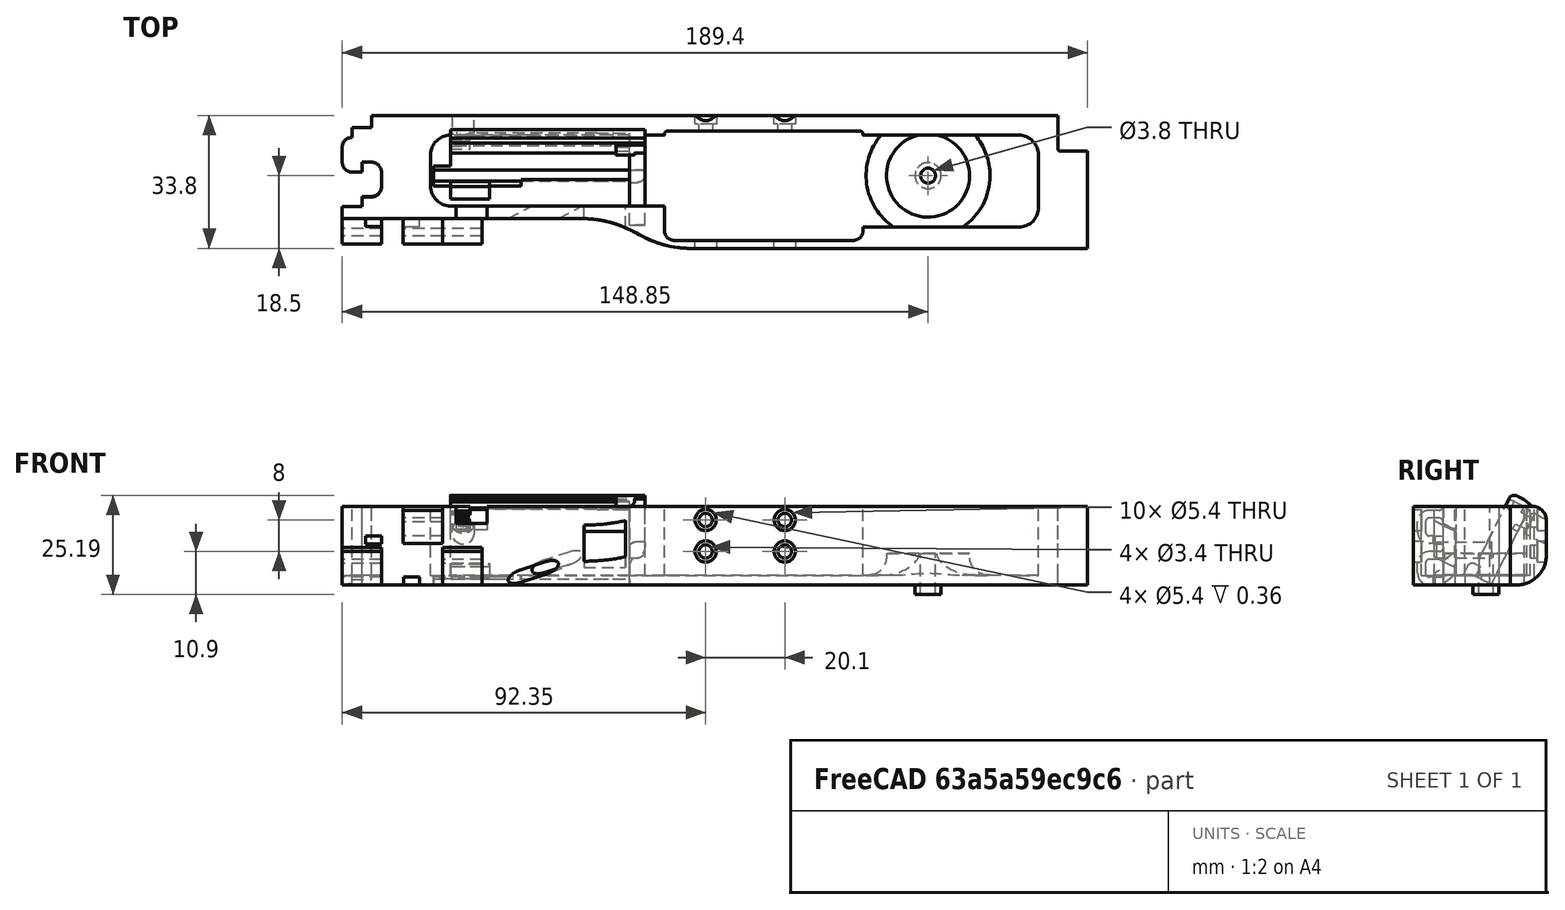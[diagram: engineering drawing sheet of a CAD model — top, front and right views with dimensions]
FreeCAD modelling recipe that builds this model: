
FCSTD DOCUMENT  (FreeCAD 0.19R0.19.2)
Label: v0_9996
License: All rights reserved
LicenseURL: http://en.wikipedia.org/wiki/All_rights_reserved
objects: Sketcher::SketchObject×45, Part::Extrusion×35, Part::MultiFuse×22, Part::Box×19, Part::Cut×16, Part::Fillet×14, App::MeasureDistance×10, Part::Cylinder×4, Part::Revolution×1, Mesh::Feature×1
note: 156 computed .brp shape members not serialized (recipe doc carries the construction recipe); baked Part::Feature solids carry a one-line shape summary decoded from their .brp

FEATURE [Sketcher::SketchObject] Sketch
  FullyConstrained = true
  sketch-geometry (36):
    g0: LineSegment StartX=0 StartY=0 StartZ=0 EndX=154.4 EndY=0 EndZ=0
    g1: LineSegment StartX=154.4 StartY=0 StartZ=0 EndX=154.4 EndY=-7.6 EndZ=0
    g2: LineSegment StartX=32.5209 StartY=-26.2 StartZ=0 EndX=-7.5 EndY=-26.2 EndZ=0
    g3-g7: Circle x5 (B-spline internal-alignment scaffolding for g8; pole/knot coordinates omitted)
    g8: BSplineCurve PolesCount=5 KnotsCount=3 Degree=3 IsPeriodic=0
    g9: GeomPoint X=61.85 Y=-33.8 Z=0
    g10: GeomPoint X=47.185 Y=-29.9 Z=0
    g11: GeomPoint X=32.5209 Y=-26.2 Z=0
    g12: Circle CenterX=121.35 CenterY=-14.3 CenterZ=0 NormalX=0 NormalY=0 NormalZ=1 AngleXU=0 Radius=3.25
    g13: LineSegment StartX=-7.5 StartY=-26.2 StartZ=0 EndX=-27.5 EndY=-26.2 EndZ=0
    g14: LineSegment StartX=-20 StartY=0 StartZ=0 EndX=0 EndY=0 EndZ=0
    g15: LineSegment StartX=-25 StartY=-3.1 StartZ=0 EndX=-20 EndY=-3.1 EndZ=0
    g16: LineSegment StartX=-25 StartY=-3.1 StartZ=0 EndX=-25 EndY=-5.6 EndZ=0
    g17: LineSegment StartX=-27.5 StartY=-8.1 StartZ=0 EndX=-27.5 EndY=-11.85 EndZ=0
    g18: ArcOfCircle CenterX=-25 CenterY=-8.1 CenterZ=0 NormalX=0 NormalY=0 NormalZ=1 AngleXU=0 Radius=2.5 StartAngle=1.5708 EndAngle=3.14159
    g19: LineSegment StartX=-25 StartY=-14.35 StartZ=0 EndX=-22.5 EndY=-14.35 EndZ=0
    g20: ArcOfCircle CenterX=-25 CenterY=-11.85 CenterZ=0 NormalX=0 NormalY=0 NormalZ=1 AngleXU=0 Radius=2.5 StartAngle=3.14159 EndAngle=4.71239
    g21: LineSegment StartX=-22.5 StartY=-14.35 StartZ=0 EndX=-22.5 EndY=-11.85 EndZ=0
    g22: LineSegment StartX=-22.5 StartY=-11.85 StartZ=0 EndX=-20 EndY=-11.85 EndZ=0
    g23: ArcOfCircle CenterX=-20 CenterY=-14.35 CenterZ=0 NormalX=0 NormalY=0 NormalZ=1 AngleXU=0 Radius=2.5 StartAngle=8e-16 EndAngle=1.5708
    g24: LineSegment StartX=-17.5 StartY=-14.35 StartZ=0 EndX=-17.5 EndY=-18.1 EndZ=0
    g25: ArcOfCircle CenterX=-20 CenterY=-18.1 CenterZ=0 NormalX=0 NormalY=0 NormalZ=1 AngleXU=0 Radius=2.5 StartAngle=4.71239 EndAngle=6.28319
    g26: LineSegment StartX=-22.5 StartY=-20.6 StartZ=0 EndX=-20 EndY=-20.6 EndZ=0
    g27: LineSegment StartX=-22.5 StartY=-20.6 StartZ=0 EndX=-22.5 EndY=-23.1 EndZ=0
    g28: LineSegment StartX=-27.5 StartY=-23.1 StartZ=0 EndX=-22.5 EndY=-23.1 EndZ=0
    g29: LineSegment StartX=-20 StartY=-3.1 StartZ=0 EndX=-20 EndY=0 EndZ=0
    g30: LineSegment StartX=-27.5 StartY=-23.1 StartZ=0 EndX=-27.5 EndY=-26.2 EndZ=0
    g31: LineSegment StartX=154.4 StartY=-7.6 StartZ=0 EndX=154.4 EndY=-8.6 EndZ=0
    g32: ArcOfCircle CenterX=154.9 CenterY=-8.6 CenterZ=0 NormalX=0 NormalY=0 NormalZ=1 AngleXU=0 Radius=0.5 StartAngle=3.14159 EndAngle=4.71239
    g33: LineSegment StartX=154.9 StartY=-9.1 StartZ=0 EndX=161.9 EndY=-9.1 EndZ=0
    g34: LineSegment StartX=161.9 StartY=-9.1 StartZ=0 EndX=161.9 EndY=-33.8 EndZ=0
    g35: LineSegment StartX=161.9 StartY=-33.8 StartZ=0 EndX=61.85 EndY=-33.8 EndZ=0
  constraints (72):
    c: PointOnObject(g0,g-2)
    c: Horizontal(g0)
    c: Distance(g0) = 154.4
    c: DistanceY(g-1,g0) = 0
    c: Vertical(g1)
    c: Distance(g1) = 7.6
    c: Coincident(g1,g0)
    c: Horizontal(g2)
    c: Block(g2)
    c: Weight(g3) = 1
    c: Coincident(g8,g2)
    c: InternalAlignment(g3-g7 -> g8) x5
    c: InternalAlignment(g9,g8)
    c: InternalAlignment(g10,g8)
    c: InternalAlignment(g11,g8)
    c: Block(g12)
    c: Coincident(g13,g2)
    c: Horizontal(g13)
    c: Distance(g13) = 20
    c: Horizontal(g14)
    c: Distance(g14) = 20
    c: Coincident(g14,g0)
    c: Horizontal(g15)
    c: Vertical(g16)
    c: Coincident(g16,g15)
    c: Vertical(g17)
    c: Coincident(g18,g16)
    c: Block(g18)
    c: Coincident(g17,g18)
    c: Horizontal(g19)
    c: Coincident(g20,g17)
    c: Block(g20)
    c: Block(g19)
    c: Vertical(g21)
    c: Coincident(g21,g19)
    c: Horizontal(g22)
    c: Coincident(g22,g21)
    c: Coincident(g23,g22)
    c: Vertical(g24)
    c: Block(g23)
    c: Coincident(g24,g23)
    c: Coincident(g25,g24)
    c: Block(g25)
    c: Horizontal(g26)
    c: Coincident(g26,g25)
    c: Vertical(g27)
    c: Coincident(g27,g26)
    c: Horizontal(g28)
    c: Coincident(g28,g27)
    c: Block(g15)
    c: Block(g28)
    c: Coincident(g29,g15)
    c: Coincident(g29,g14)
    c: Vertical(g29)
    c: Coincident(g30,g28)
    c: Coincident(g30,g13)
    c: Vertical(g30)
    c: Vertical(g31)
    c: Distance(g31) = 1
    c: Coincident(g31,g1)
    c: Coincident(g32,g31)
    c: Block(g32)
    c: Coincident(g33,g32)
    c: Horizontal(g33)
    c: Coincident(g34,g33)
    c: Vertical(g34)
    c: Block(g34)
    c: Coincident(g35,g34)
    c: Horizontal(g35)
    c: Block(g35)
    c: Coincident(g8,g35)
    c: Block(g8)
FEATURE [Part::Extrusion] Extrude  label="mainBodyBaseExtrude"
  Base = -> Sketch
  Dir = (0,0,1)
  DirMode = 2
  FaceMakerClass = Part::FaceMakerBullseye
  LengthFwd = 2.4
  LengthRev = 0
  Solid = true
  Symmetric = false
FEATURE [Sketcher::SketchObject] Sketch001
  FullyConstrained = true
  sketch-geometry (75):
    g0: ArcOfCircle CenterX=144.4 CenterY=-10 CenterZ=0 NormalX=0 NormalY=0 NormalZ=1 AngleXU=0 Radius=5 StartAngle=4.345e-13 EndAngle=1.5708
    g1: LineSegment StartX=32.5209 StartY=-26.2 StartZ=0 EndX=-7.49911 EndY=-26.2 EndZ=0
    g2: LineSegment StartX=0 StartY=0 StartZ=0 EndX=154.4 EndY=0 EndZ=0
    g3-g7: Circle x5 (B-spline internal-alignment scaffolding for g8; pole/knot coordinates omitted)
    g8: BSplineCurve PolesCount=5 KnotsCount=3 Degree=3 IsPeriodic=0
    g9: GeomPoint X=61.85 Y=-33.8 Z=0
    g10: GeomPoint X=47.1857 Y=-29.9 Z=0
    g11: GeomPoint X=32.5209 Y=-26.2 Z=0
    g12: LineSegment StartX=154.4 StartY=0 StartZ=0 EndX=154.4 EndY=-7.6 EndZ=0
    g13: LineSegment StartX=20 StartY=-5 StartZ=0 EndX=54.35 EndY=-5 EndZ=0
    g14: LineSegment StartX=104.85 StartY=-5 StartZ=0 EndX=144.4 EndY=-5 EndZ=0
    g15: LineSegment StartX=54.35 StartY=-23 StartZ=0 EndX=20 EndY=-23 EndZ=0
    g16: LineSegment StartX=-27.4991 StartY=-26.2 StartZ=0 EndX=-7.49911 EndY=-26.2 EndZ=0
    g17: LineSegment StartX=-20 StartY=0 StartZ=0 EndX=0 EndY=0 EndZ=0
    g18: LineSegment StartX=-27.4991 StartY=-23.2 StartZ=0 EndX=-22.5 EndY=-23.2 EndZ=0
    g19: LineSegment StartX=-22.5 StartY=-20.7 StartZ=0 EndX=-22.5 EndY=-23.2 EndZ=0
    g20: LineSegment StartX=-22.5 StartY=-20.7 StartZ=0 EndX=-20 EndY=-20.7 EndZ=0
    g21: ArcOfCircle CenterX=-20 CenterY=-18.2 CenterZ=0 NormalX=0 NormalY=0 NormalZ=1 AngleXU=0 Radius=2.5 StartAngle=4.71239 EndAngle=6.28319
    g22: LineSegment StartX=-17.5 StartY=-14.4 StartZ=0 EndX=-17.5 EndY=-18.2 EndZ=0
    g23: ArcOfCircle CenterX=-20 CenterY=-14.4 CenterZ=0 NormalX=0 NormalY=0 NormalZ=1 AngleXU=0 Radius=2.5 StartAngle=9e-16 EndAngle=1.5708
    g24: LineSegment StartX=-22.5 StartY=-11.9 StartZ=0 EndX=-20 EndY=-11.9 EndZ=0
    g25: LineSegment StartX=-22.5 StartY=-14.4 StartZ=0 EndX=-22.5 EndY=-11.9 EndZ=0
    g26: LineSegment StartX=-25 StartY=-14.4 StartZ=0 EndX=-22.5 EndY=-14.4 EndZ=0
    g27: ArcOfCircle CenterX=-25 CenterY=-11.9 CenterZ=0 NormalX=0 NormalY=0 NormalZ=1 AngleXU=0 Radius=2.5 StartAngle=3.14159 EndAngle=4.71239
    g28: LineSegment StartX=-27.5 StartY=-8.1 StartZ=0 EndX=-27.5 EndY=-11.9 EndZ=0
    g29: ArcOfCircle CenterX=-25 CenterY=-8.1 CenterZ=0 NormalX=0 NormalY=0 NormalZ=1 AngleXU=0 Radius=2.5 StartAngle=1.5708 EndAngle=3.14159
    g30: LineSegment StartX=-25 StartY=-3.1 StartZ=0 EndX=-25 EndY=-5.6 EndZ=0
    g31: LineSegment StartX=-20 StartY=-3.1 StartZ=0 EndX=-25 EndY=-3.1 EndZ=0
    g32: LineSegment StartX=-20 StartY=0 StartZ=0 EndX=-20 EndY=-3.1 EndZ=0
    g33: LineSegment StartX=-27.4991 StartY=-26.2 StartZ=0 EndX=-27.4991 EndY=-23.2 EndZ=0
    g34: LineSegment StartX=4.09e-14 StartY=-5 StartZ=0 EndX=20 EndY=-5 EndZ=0
    g35: ArcOfCircle CenterX=7.1e-15 CenterY=-18 CenterZ=0 NormalX=0 NormalY=0 NormalZ=1 AngleXU=0 Radius=5 StartAngle=3.14159 EndAngle=4.71239
    g36: ArcOfCircle CenterX=4.26e-14 CenterY=-10 CenterZ=0 NormalX=0 NormalY=0 NormalZ=1 AngleXU=0 Radius=5 StartAngle=1.5708 EndAngle=3.14159
    g37: LineSegment StartX=-5 StartY=-18 StartZ=0 EndX=-5 EndY=-10 EndZ=0
    g38: LineSegment StartX=6.2e-15 StartY=-23 StartZ=0 EndX=20 EndY=-23 EndZ=0
    g39: LineSegment StartX=154.4 StartY=-7.6 StartZ=0 EndX=154.4 EndY=-8.6 EndZ=0
    g40: LineSegment StartX=154.9 StartY=-9.1 StartZ=0 EndX=161.9 EndY=-9.1 EndZ=0
    g41: ArcOfCircle CenterX=154.9 CenterY=-8.6 CenterZ=0 NormalX=0 NormalY=0 NormalZ=1 AngleXU=0 Radius=0.5 StartAngle=3.14159 EndAngle=4.71299
    g42: LineSegment StartX=104.85 StartY=-28.3916 StartZ=0 EndX=144.408 EndY=-28.3916 EndZ=0
    g43: LineSegment StartX=149.4 StartY=-10 StartZ=0 EndX=149.4 EndY=-23.4 EndZ=0
    g44: ArcOfCircle CenterX=144.408 CenterY=-23.4 CenterZ=0 NormalX=0 NormalY=0 NormalZ=1 AngleXU=0 Radius=4.99164 StartAngle=4.71239 EndAngle=6.28319
    g45: LineSegment StartX=104.85 StartY=-28.3916 StartZ=0 EndX=104.85 EndY=-28.7833 EndZ=0
    g46: LineSegment StartX=54.35 StartY=-28.7916 StartZ=0 EndX=54.35 EndY=-23 EndZ=0
    g47: LineSegment StartX=161.9 StartY=-33.8 StartZ=0 EndX=161.9 EndY=-9.1 EndZ=0
    g48: LineSegment StartX=61.85 StartY=-33.8 StartZ=0 EndX=161.9 EndY=-33.8 EndZ=0
    g49: Circle CenterX=54.35 CenterY=-28.7916 CenterZ=0 NormalX=0 NormalY=0 NormalZ=1 AngleXU=0 Radius=1
    g50: Circle CenterX=54.35 CenterY=-31.7916 CenterZ=0 NormalX=0 NormalY=0 NormalZ=1 AngleXU=0 Radius=1
    g51: Circle CenterX=57.35 CenterY=-31.7916 CenterZ=0 NormalX=0 NormalY=0 NormalZ=1 AngleXU=0 Radius=1
    g52: BSplineCurve PolesCount=3 KnotsCount=2 Degree=2 IsPeriodic=0
    g53: GeomPoint X=54.35 Y=-28.7916 Z=0
    g54: GeomPoint X=57.35 Y=-31.7916 Z=0
    g55: Circle CenterX=104.85 CenterY=-28.7833 CenterZ=0 NormalX=0 NormalY=0 NormalZ=1 AngleXU=0 Radius=1
    g56: Circle CenterX=104.85 CenterY=-31.7916 CenterZ=0 NormalX=0 NormalY=0 NormalZ=1 AngleXU=0 Radius=1
    g57: Circle CenterX=101.85 CenterY=-31.7916 CenterZ=0 NormalX=0 NormalY=0 NormalZ=1 AngleXU=0 Radius=1
    g58: BSplineCurve PolesCount=3 KnotsCount=2 Degree=2 IsPeriodic=0
    g59: GeomPoint X=104.85 Y=-28.7833 Z=0
    g60: GeomPoint X=101.85 Y=-31.7916 Z=0
    g61: LineSegment StartX=57.35 StartY=-31.7916 StartZ=0 EndX=101.85 EndY=-31.7916 EndZ=0
    g62: Circle CenterX=54.35 CenterY=-5 CenterZ=0 NormalX=0 NormalY=0 NormalZ=1 AngleXU=0 Radius=1
    g63: Circle CenterX=54.35 CenterY=-4 CenterZ=0 NormalX=0 NormalY=0 NormalZ=1 AngleXU=0 Radius=1
    g64: Circle CenterX=55.15 CenterY=-4 CenterZ=0 NormalX=0 NormalY=0 NormalZ=1 AngleXU=0 Radius=1
    g65: BSplineCurve PolesCount=3 KnotsCount=2 Degree=2 IsPeriodic=0
    g66: GeomPoint X=54.35 Y=-5 Z=0
    g67: GeomPoint X=55.15 Y=-4 Z=0
    g68: Circle CenterX=104.85 CenterY=-5 CenterZ=0 NormalX=0 NormalY=0 NormalZ=1 AngleXU=0 Radius=1
    g69: Circle CenterX=104.85 CenterY=-4 CenterZ=0 NormalX=0 NormalY=0 NormalZ=1 AngleXU=0 Radius=1
    g70: Circle CenterX=104.05 CenterY=-4 CenterZ=0 NormalX=0 NormalY=0 NormalZ=1 AngleXU=0 Radius=1
    g71: BSplineCurve PolesCount=3 KnotsCount=2 Degree=2 IsPeriodic=0
    g72: GeomPoint X=104.85 Y=-5 Z=0
    g73: GeomPoint X=104.05 Y=-4 Z=0
    g74: LineSegment StartX=104.05 StartY=-4 StartZ=0 EndX=55.15 EndY=-4 EndZ=0
  constraints (156):
    c: PointOnObject(g2,g-2)
    c: DistanceY(g-1,g2) = 0
    c: Block(g0)
    c: Horizontal(g1)
    c: Distance(g1) = 40.02
    c: Horizontal(g2)
    c: Block(g2)
    c: Weight(g3) = 1
    c: Equal(g3, g4-g7) x4
    c: Coincident(g8,g1)
    c: InternalAlignment(g3-g7 -> g8) x5
    c: InternalAlignment(g9,g8)
    c: InternalAlignment(g10,g8)
    c: InternalAlignment(g11,g8)
    c: Vertical(g12)
    c: Coincident(g12,g2)
    c: Distance(g12) = 7.6
    c: Block(g12)
    c: Horizontal(g13)
    c: Coincident(g14,g0)
    c: Horizontal(g14)
    c: Horizontal(g15)
    c: Horizontal(g16)
    c: Distance(g16) = 20
    c: Coincident(g1,g16)
    c: Horizontal(g17)
    c: Distance(g17) = 20
    c: Coincident(g17,g2)
    c: Horizontal(g31)
    c: Vertical(g30)
    c: Coincident(g29,g30)
    c: Vertical(g28)
    c: Block(g29)
    c: Coincident(g27,g28)
    c: Block(g27)
    c: Horizontal(g26)
    c: Coincident(g26,g27)
    c: Vertical(g25)
    c: Coincident(g25,g26)
    c: Horizontal(g24)
    c: Coincident(g23,g24)
    c: Block(g23)
    c: Vertical(g22)
    c: Coincident(g21,g22)
    c: Block(g21)
    c: Horizontal(g20)
    c: Coincident(g20,g21)
    c: Vertical(g19)
    c: Coincident(g19,g20)
    c: Horizontal(g18)
    c: Coincident(g18,g19)
    c: Coincident(g32,g17)
    c: Coincident(g32,g31)
    c: Vertical(g32)
    c: Coincident(g33,g16)
    c: Coincident(g33,g18)
    c: Vertical(g33)
    c: Block(g33)
    c: Block(g18)
    c: Block(g22)
    c: Block(g26)
    c: Block(g25)
    c: Block(g24)
    c: Block(g28)
    c: Block(g31)
    c: Block(g30)
    c: Horizontal(g34)
    c: Distance(g34) = 20
    c: Block(g35)
    c: Block(g36)
    c: Coincident(g37,g35)
    c: Coincident(g37,g36)
    c: Vertical(g37)
    c: Coincident(g38,g35)
    c: Coincident(g38,g15)
    c: Horizontal(g38)
    c: Block(g38)
    c: Block(g34)
    c: Block(g13)
    c: Vertical(g39)
    c: Distance(g39) = 1
    c: Coincident(g39,g12)
    c: Horizontal(g40)
    c: Coincident(g41,g39)
    c: Coincident(g41,g40)
    c: Block(g39)
    c: Block(g41)
    c: Horizontal(g42)
    c: Vertical(g43)
    c: Distance(g43) = 13.4
    c: Coincident(g43,g0)
    c: Block(g42)
    c: Block(g43)
    c: Coincident(g44,g43)
    c: Coincident(g44,g42)
    c: Block(g44)
    c: Distance(g15) = 34.35
    c: Coincident(g45,g42)
    c: Vertical(g45)
    c: Coincident(g46,g15)
    c: Vertical(g46)
    c: Coincident(g47,g40)
    c: Vertical(g47)
    c: Block(g47)
    c: Coincident(g48,g47)
    c: Horizontal(g48)
    c: Block(g48)
    c: Coincident(g8,g48)
    c: Block(g8)
    c: Coincident(g52,g46)
    c: Weight(g49) = 1
    c: Equal(g49,g50)
    c: Equal(g49,g51)
    c: InternalAlignment(g49,g52)
    c: InternalAlignment(g50,g52)
    c: InternalAlignment(g51,g52)
    c: InternalAlignment(g53,g52)
    c: InternalAlignment(g54,g52)
    c: Coincident(g58,g45)
    c: Weight(g55) = 1
    c: Equal(g55,g56)
    c: Equal(g55,g57)
    c: InternalAlignment(g55,g58)
    c: InternalAlignment(g56,g58)
    c: InternalAlignment(g57,g58)
    c: InternalAlignment(g59,g58)
    c: InternalAlignment(g60,g58)
    c: Block(g58)
    c: Block(g52)
    c: Coincident(g61,g52)
    c: Coincident(g61,g58)
    c: Horizontal(g61)
    c: Block(g14)
    c: Coincident(g65,g13)
    c: Weight(g62) = 1
    c: Equal(g62,g63)
    c: Equal(g62,g64)
    c: InternalAlignment(g62,g65)
    c: InternalAlignment(g63,g65)
    c: InternalAlignment(g64,g65)
    c: InternalAlignment(g66,g65)
    c: InternalAlignment(g67,g65)
    c: Block(g65)
    c: Coincident(g71,g14)
    c: Weight(g68) = 1
    c: Equal(g68,g69)
    c: Equal(g68,g70)
    c: InternalAlignment(g68,g71)
    c: InternalAlignment(g69,g71)
    c: InternalAlignment(g70,g71)
    c: InternalAlignment(g72,g71)
    c: InternalAlignment(g73,g71)
    c: Block(g71)
    c: Coincident(g74,g71)
    c: Coincident(g74,g65)
    c: Horizontal(g74)
FEATURE [Sketcher::SketchObject] Sketch005
  FullyConstrained = true
  Placement = pos=(0,0,0) rot=(1,0,0;1.5708rad)
  sketch-geometry (4):
    g0: Circle CenterX=84.95 CenterY=16.5 CenterZ=0 NormalX=0 NormalY=0 NormalZ=1 AngleXU=0 Radius=1.7
    g1: Circle CenterX=84.95 CenterY=8.5 CenterZ=0 NormalX=0 NormalY=0 NormalZ=1 AngleXU=0 Radius=1.7
    g2: Circle CenterX=64.85 CenterY=8.5 CenterZ=0 NormalX=0 NormalY=0 NormalZ=1 AngleXU=0 Radius=1.7
    g3: Circle CenterX=64.85 CenterY=16.5 CenterZ=0 NormalX=0 NormalY=0 NormalZ=1 AngleXU=0 Radius=1.7
  constraints (4):
    c: Block(g0)
    c: Block(g1)
    c: Block(g2)
    c: Block(g3)
FEATURE [Part::Extrusion] Extrude004  label="removeFromMainBodyToCreateScrewHolesForSolenoidExtrude004"
  Base = -> Sketch005
  Dir = (0,-1,1.1e-15)
  DirMode = 2
  FaceMakerClass = Part::FaceMakerBullseye
  LengthFwd = 10
  LengthRev = 0
  Solid = true
  Symmetric = false
FEATURE [Sketcher::SketchObject] Sketch004
  FullyConstrained = true
  Placement = pos=(0,0,0) rot=(1,0,0;1.5708rad)
  sketch-geometry (12):
    g0: LineSegment StartX=15.75 StartY=2.5 StartZ=0 EndX=15.75 EndY=0 EndZ=0
    g1: Circle CenterX=15.75 CenterY=2.5 CenterZ=0 NormalX=0 NormalY=0 NormalZ=1 AngleXU=0 Radius=1
    g2: Circle CenterX=10.55 CenterY=2.5 CenterZ=0 NormalX=0 NormalY=0 NormalZ=1 AngleXU=0 Radius=1
    g3: Circle CenterX=10.55 CenterY=8 CenterZ=0 NormalX=0 NormalY=0 NormalZ=1 AngleXU=0 Radius=1
    g4: BSplineCurve PolesCount=3 KnotsCount=2 Degree=2 IsPeriodic=0
    g5: GeomPoint X=15.75 Y=2.5 Z=0
    g6: GeomPoint X=10.55 Y=8 Z=0
    g7: LineSegment StartX=1.9 StartY=8 StartZ=0 EndX=10.55 EndY=8 EndZ=0
    g8: LineSegment StartX=1.9 StartY=-2.4 StartZ=0 EndX=1.9 EndY=8 EndZ=0
    g9: LineSegment StartX=3.30092 StartY=-2.4 StartZ=0 EndX=3.30092 EndY=0 EndZ=0
    g10: LineSegment StartX=15.75 StartY=0 StartZ=0 EndX=3.30092 EndY=0 EndZ=0
    g11: LineSegment StartX=3.30092 StartY=-2.4 StartZ=0 EndX=1.9 EndY=-2.4 EndZ=0
  constraints (26):
    c: Vertical(g0)
    c: Distance(g0) = 2.5
    c: Coincident(g4,g0)
    c: Weight(g1) = 1
    c: Equal(g1,g2)
    c: Equal(g1,g3)
    c: InternalAlignment(g1,g4)
    c: InternalAlignment(g2,g4)
    c: InternalAlignment(g3,g4)
    c: InternalAlignment(g5,g4)
    c: InternalAlignment(g6,g4)
    c: Block(g4)
    c: Coincident(g7,g4)
    c: Horizontal(g7)
    c: Vertical(g8)
    c: Coincident(g8,g7)
    c: Block(g8)
    c: Vertical(g9)
    c: Coincident(g10,g0)
    c: PointOnObject(g10,g-1)
    c: Horizontal(g10)
    c: Coincident(g10,g9)
    c: Block(g9)
    c: Coincident(g11,g9)
    c: Coincident(g11,g8)
    c: Horizontal(g11)
FEATURE [Sketcher::SketchObject] Sketch007
  FullyConstrained = true
  Placement = pos=(0,-14.3,2.37) rot=(-1,0,0;2.03453rad)
  sketch-geometry (6):
    g0: LineSegment StartX=0 StartY=0 StartZ=0 EndX=45.5 EndY=0 EndZ=0
    g1: LineSegment StartX=0 StartY=0 StartZ=0 EndX=0 EndY=-21.2 EndZ=0
    g2: LineSegment StartX=45.5 StartY=0 StartZ=0 EndX=49.5 EndY=0 EndZ=0
    g3: LineSegment StartX=49.5 StartY=0 StartZ=0 EndX=49.5 EndY=-21.2 EndZ=0
    g4: LineSegment StartX=49.5 StartY=-21.2 StartZ=0 EndX=0 EndY=-21.2 EndZ=0
    g5: Circle CenterX=3.25 CenterY=-18.05 CenterZ=0 NormalX=0 NormalY=0 NormalZ=1 AngleXU=0 Radius=1.6
  constraints (15):
    c: Coincident(g0,g-1)
    c: Horizontal(g0)
    c: Distance(g0) = 45.5
    c: Coincident(g1,g0)
    c: Vertical(g1)
    c: Horizontal(g2)
    c: Distance(g2) = 4
    c: Coincident(g2,g0)
    c: Coincident(g3,g2)
    c: Vertical(g3)
    c: Block(g3)
    c: Coincident(g4,g3)
    c: Horizontal(g4)
    c: Coincident(g4,g1)
    c: Block(g5)
FEATURE [Part::Extrusion] Extrude005  label="solenoidDriverHolderExtrude005"
  Base = -> Sketch007
  Dir = (0,0.894389,-0.447291)
  DirMode = 2
  FaceMakerClass = Part::FaceMakerBullseye
  LengthFwd = 10
  LengthRev = 0
  Placement = pos=(0,0,-2) rot=(0,0,1;0rad)
  Solid = true
  Symmetric = false
FEATURE [Sketcher::SketchObject] Sketch008
  FullyConstrained = false
  Placement = pos=(0,-4.3,-2.6) rot=(-1,0,0;2.03453rad)
  sketch-geometry (1):
    g0: Circle CenterX=42.25 CenterY=-3.15 CenterZ=0 NormalX=0 NormalY=0 NormalZ=1 AngleXU=0 Radius=4.5
FEATURE [Sketcher::SketchObject] Sketch009
  FullyConstrained = true
  Placement = pos=(0,-4.3,-2.6) rot=(-1,0,0;2.03453rad)
  sketch-geometry (1):
    g0: Circle CenterX=3.25 CenterY=-18.0217 CenterZ=0 NormalX=0 NormalY=0 NormalZ=1 AngleXU=0 Radius=2.8
  constraints (1):
    c: Block(g0)
FEATURE [Sketcher::SketchObject] Sketch010
  FullyConstrained = true
  Placement = pos=(0,-14.3,2.37) rot=(-1,0,0;2.03453rad)
  sketch-geometry (1):
    g0: Circle CenterX=3.25 CenterY=-18.05 CenterZ=0 NormalX=0 NormalY=0 NormalZ=1 AngleXU=0 Radius=1.6
  constraints (1):
    c: Block(g0)
FEATURE [Part::Extrusion] Extrude008  label="removeFromScrewHole3"
  Base = -> Sketch010
  Dir = (0,0.894389,-0.447291)
  DirMode = 2
  FaceMakerClass = Part::FaceMakerBullseye
  LengthFwd = -25
  LengthRev = 0
  Placement = pos=(0,4,-4) rot=(0,0,1;0rad)
  Solid = true
  Symmetric = false
FEATURE [Sketcher::SketchObject] Sketch011
  FullyConstrained = true
  Placement = pos=(0,-14.3,2.37) rot=(-1,0,0;2.03453rad)
  sketch-geometry (4):
    g0: LineSegment StartX=49.5 StartY=-21.2 StartZ=0 EndX=49.5 EndY=-22.8 EndZ=0
    g1: LineSegment StartX=49.5 StartY=-22.8 StartZ=0 EndX=0.002238 EndY=-22.8 EndZ=0
    g2: LineSegment StartX=0.002238 StartY=-21.2 StartZ=0 EndX=0.002238 EndY=-22.8 EndZ=0
    g3: LineSegment StartX=49.5 StartY=-21.2 StartZ=0 EndX=0.002238 EndY=-21.2 EndZ=0
  constraints (10):
    c: Vertical(g0)
    c: Distance(g0) = 1.6
    c: Coincident(g1,g0)
    c: Horizontal(g1)
    c: Vertical(g2)
    c: Coincident(g2,g1)
    c: Coincident(g3,g0)
    c: Coincident(g3,g2)
    c: Horizontal(g3)
    c: Block(g3)
FEATURE [Part::Extrusion] Extrude009  label="solenoidDriverTopLipFront"
  Base = -> Sketch011
  Dir = (0,0.894389,-0.447291)
  DirMode = 2
  FaceMakerClass = Part::FaceMakerBullseye
  LengthFwd = -2
  LengthRev = 0
  Placement = pos=(0,-2.9,-0.35) rot=(0,0,1;0rad)
  Solid = true
  Symmetric = false
FEATURE [Sketcher::SketchObject] Sketch012
  FullyConstrained = true
  Placement = pos=(0,-14.3,2.37) rot=(-1,0,0;2.03453rad)
  sketch-geometry (4):
    g0: LineSegment StartX=49.5 StartY=-21.2 StartZ=0 EndX=49.5 EndY=-22.8 EndZ=0
    g1: LineSegment StartX=49.5 StartY=-22.8 StartZ=0 EndX=0.002238 EndY=-22.8 EndZ=0
    g2: LineSegment StartX=0.002238 StartY=-21.2 StartZ=0 EndX=0.002238 EndY=-22.8 EndZ=0
    g3: LineSegment StartX=49.5 StartY=-21.2 StartZ=0 EndX=0.002238 EndY=-21.2 EndZ=0
  constraints (10):
    c: Vertical(g0)
    c: Distance(g0) = 1.6
    c: Coincident(g1,g0)
    c: Horizontal(g1)
    c: Vertical(g2)
    c: Coincident(g2,g1)
    c: Coincident(g3,g0)
    c: Coincident(g3,g2)
    c: Horizontal(g3)
    c: Block(g3)
FEATURE [Part::Extrusion] Extrude010  label="solenoidDriverTopLipLowerExtrude010"
  Base = -> Sketch012
  Dir = (0,0.894389,-0.447291)
  DirMode = 2
  FaceMakerClass = Part::FaceMakerBullseye
  LengthFwd = 5.05
  LengthRev = 0
  Solid = true
  Symmetric = false
FEATURE [Sketcher::SketchObject] Sketch015
  FullyConstrained = true
  Placement = pos=(0,-14.3,2.37) rot=(-1,0,0;2.03453rad)
  sketch-geometry (4):
    g0: LineSegment StartX=0 StartY=1.5 StartZ=0 EndX=0 EndY=0 EndZ=0
    g1: LineSegment StartX=0 StartY=1.5 StartZ=0 EndX=5 EndY=1.5 EndZ=0
    g2: LineSegment StartX=5 StartY=1.5 StartZ=0 EndX=5 EndY=0 EndZ=0
    g3: LineSegment StartX=0 StartY=0 StartZ=0 EndX=5 EndY=0 EndZ=0
  constraints (13):
    c: Vertical(g0)
    c: Distance(g0) = 1.5
    c: Horizontal(g1)
    c: Distance(g1) = 5
    c: Coincident(g1,g0)
    c: Vertical(g2)
    c: Distance(g2) = 1.5
    c: Coincident(g2,g1)
    c: Block(g1)
    c: Block(g2)
    c: Block(g0)
    c: Coincident(g3,g0)
    c: Coincident(g3,g2)
FEATURE [Part::Extrusion] Extrude013  label="solenoidDriverBottomLipTopExtrude012"
  Base = -> Sketch015
  Dir = (0,0.894389,-0.447291)
  DirMode = 2
  FaceMakerClass = Part::FaceMakerBullseye
  LengthFwd = -6.5
  LengthRev = 0
  Placement = pos=(0,-14.15,19.65) rot=(1,0,0;1.5708rad)
  Solid = true
  Symmetric = false
FEATURE [Sketcher::SketchObject] Sketch016
  FullyConstrained = true
  Placement = pos=(0,0,0) rot=(1,0,0;1.5708rad)
  sketch-geometry (4):
    g0: Circle CenterX=84.15 CenterY=16.5 CenterZ=0 NormalX=0 NormalY=0 NormalZ=1 AngleXU=0 Radius=2.7
    g1: Circle CenterX=64.05 CenterY=16.5 CenterZ=0 NormalX=0 NormalY=0 NormalZ=1 AngleXU=0 Radius=2.7
    g2: Circle CenterX=64.05 CenterY=8.5 CenterZ=0 NormalX=0 NormalY=0 NormalZ=1 AngleXU=0 Radius=2.7
    g3: Circle CenterX=84.15 CenterY=8.5 CenterZ=0 NormalX=0 NormalY=0 NormalZ=1 AngleXU=0 Radius=2.7
  constraints (4):
    c: Block(g0)
    c: Block(g1)
    c: Block(g3)
    c: Block(g2)
FEATURE [Part::Extrusion] Extrude014  label="removeFromMainBodyToCreateScrewHoleCounterSinks"
  Base = -> Sketch016
  Dir = (0,-1,1.1e-15)
  DirMode = 2
  FaceMakerClass = Part::FaceMakerBullseye
  LengthFwd = 1.9
  LengthRev = 0
  Placement = pos=(0.8,-0.36,0) rot=(0,0,1;0rad)
  Solid = true
  Symmetric = false
FEATURE [Part::Extrusion] Extrude015  label="removeFromScrewHole2Extrude007"
  Base = -> Sketch009
  Dir = (0,0.894389,-0.447291)
  DirMode = 2
  FaceMakerClass = Part::FaceMakerBullseye
  LengthFwd = 10
  LengthRev = 0
  Placement = pos=(0,-8,2) rot=(0,0,1;0rad)
  Solid = true
  Symmetric = false
FEATURE [Sketcher::SketchObject] Sketch017
  FullyConstrained = true
  Placement = pos=(0,-14.3,2.37) rot=(-1,0,0;2.03453rad)
  sketch-geometry (4):
    g0: LineSegment StartX=0 StartY=1.5 StartZ=0 EndX=0 EndY=0 EndZ=0
    g1: LineSegment StartX=0 StartY=1.5 StartZ=0 EndX=5 EndY=1.5 EndZ=0
    g2: LineSegment StartX=5 StartY=1.5 StartZ=0 EndX=5 EndY=0 EndZ=0
    g3: LineSegment StartX=0 StartY=0 StartZ=0 EndX=5 EndY=0 EndZ=0
  constraints (13):
    c: Vertical(g0)
    c: Distance(g0) = 1.5
    c: Horizontal(g1)
    c: Distance(g1) = 5
    c: Coincident(g1,g0)
    c: Vertical(g2)
    c: Distance(g2) = 1.5
    c: Coincident(g2,g1)
    c: Block(g1)
    c: Block(g2)
    c: Block(g0)
    c: Coincident(g3,g0)
    c: Coincident(g3,g2)
FEATURE [Part::Extrusion] Extrude016  label="solenoidDriverBottomLipTopExtrude013"
  Base = -> Sketch017
  Dir = (0,0.894389,-0.447291)
  DirMode = 2
  FaceMakerClass = Part::FaceMakerBullseye
  LengthFwd = -6.5
  LengthRev = 0
  Placement = pos=(0,-15.45,20.3) rot=(1,0,0;1.5708rad)
  Solid = true
  Symmetric = false
FEATURE [Part::Fillet] Fillet005  label="solenoidDriverBottomLipTopFillet005"
  Base = -> Extrude016
  Edges = 1 edges r=1.4: [Edge6]
FEATURE [Sketcher::SketchObject] Sketch018
  FullyConstrained = true
  Placement = pos=(38.5,-14.3,2.37) rot=(-1,0,0;2.03453rad)
  sketch-geometry (4):
    g0: LineSegment StartX=11 StartY=0 StartZ=0 EndX=11 EndY=1.5 EndZ=0
    g1: LineSegment StartX=11 StartY=0 StartZ=0 EndX=3.6 EndY=0 EndZ=0
    g2: LineSegment StartX=3.6 StartY=0 StartZ=0 EndX=3.6 EndY=1.5 EndZ=0
    g3: LineSegment StartX=11 StartY=1.5 StartZ=0 EndX=3.6 EndY=1.5 EndZ=0
  constraints (12):
    c: PointOnObject(g0,g-1)
    c: Vertical(g0)
    c: Distance(g0) = 1.5
    c: Horizontal(g1)
    c: Distance(g1) = 7.4
    c: Coincident(g1,g0)
    c: Block(g0)
    c: Coincident(g2,g1)
    c: Vertical(g2)
    c: Coincident(g3,g0)
    c: Horizontal(g3)
    c: Coincident(g2,g3)
FEATURE [Part::Extrusion] Extrude017
  Base = -> Sketch018
  Dir = (0,0.894389,-0.447291)
  DirMode = 2
  FaceMakerClass = Part::FaceMakerBullseye
  LengthFwd = 4
  LengthRev = 0
  Placement = pos=(0,-8.212,34.025) rot=(1,0,0;1.5708rad)
  Solid = true
  Symmetric = false
FEATURE [Sketcher::SketchObject] Sketch019
  FullyConstrained = true
  Placement = pos=(0,0,0) rot=(1,0,0;1.5708rad)
  sketch-geometry (4):
    g0: Circle CenterX=84.95 CenterY=8.5 CenterZ=0 NormalX=0 NormalY=0 NormalZ=1 AngleXU=0 Radius=2.7
    g1: Circle CenterX=64.85 CenterY=8.5 CenterZ=0 NormalX=0 NormalY=0 NormalZ=1 AngleXU=0 Radius=2.7
    g2: Circle CenterX=64.85 CenterY=16.5 CenterZ=0 NormalX=0 NormalY=0 NormalZ=1 AngleXU=0 Radius=2.7
    g3: Circle CenterX=84.95 CenterY=16.5 CenterZ=0 NormalX=0 NormalY=0 NormalZ=1 AngleXU=0 Radius=2.7
  constraints (4):
    c: Block(g3)
    c: Block(g2)
    c: Block(g0)
    c: Block(g1)
FEATURE [Part::Extrusion] Extrude019  label="removeSolenoidAdjusterHoles"
  Base = -> Sketch019
  Dir = (0,-1,1.1e-15)
  DirMode = 2
  FaceMakerClass = Part::FaceMakerBullseye
  LengthFwd = 6
  LengthRev = 0
  Placement = pos=(0,-30,0) rot=(0,0,1;0rad)
  Solid = true
  Symmetric = false
FEATURE [Sketcher::SketchObject] Sketch020
  FullyConstrained = true
  Placement = pos=(0,-14.3,2.37) rot=(-1,0,0;2.03453rad)
  sketch-geometry (6):
    g0: LineSegment StartX=45.5 StartY=-21.2 StartZ=0 EndX=49.5 EndY=-21.2 EndZ=0
    g1: LineSegment StartX=45.5 StartY=0 StartZ=0 EndX=49.5 EndY=0 EndZ=0
    g2: LineSegment StartX=49.5 StartY=0 StartZ=0 EndX=49.5 EndY=-21.2 EndZ=0
    g3: LineSegment StartX=4 StartY=0 StartZ=0 EndX=4 EndY=-21.2 EndZ=0
    g4: LineSegment StartX=45.5 StartY=-21.2 StartZ=0 EndX=4 EndY=-21.2 EndZ=0
    g5: LineSegment StartX=4 StartY=0 StartZ=0 EndX=45.5 EndY=0 EndZ=0
  constraints (16):
    c: Horizontal(g0)
    c: Distance(g0) = 4
    c: Horizontal(g1)
    c: Distance(g1) = 4
    c: Coincident(g2,g1)
    c: Coincident(g2,g0)
    c: Vertical(g2)
    c: Block(g2)
    c: Vertical(g3)
    c: Coincident(g4,g0)
    c: Horizontal(g4)
    c: Coincident(g4,g3)
    c: Coincident(g5,g1)
    c: Horizontal(g5)
    c: Block(g3)
    c: Block(g5)
FEATURE [Part::Box] Box  label="Cube"
  AttacherType = Attacher::AttachEngine3D
  Height = 10
  Length = 190
  Placement = pos=(-30,0,0) rot=(0,0,1;0rad)
  Width = 10
FEATURE [Part::Fillet] Fillet008
  Base = -> Box
  Edges = 1 edges r=7.5: [Edge11]
FEATURE [Part::Box] Box001  label="Cube001"
  AttacherType = Attacher::AttachEngine3D
  Height = 10
  Length = 190
  Placement = pos=(-35,0,0) rot=(0,0,1;0rad)
  Width = 10
FEATURE [Part::Cut] Cut  label="filletMain"
  Base = -> Box001
  Placement = pos=(0,-10,0) rot=(0,0,1;0rad)
  Tool = -> Fillet008
FEATURE [Part::Box] Box002  label="Cube002"
  AttacherType = Attacher::AttachEngine3D
  Height = 30
  Length = 190
  Placement = pos=(-20,0,0) rot=(0,0,1;0rad)
  Width = 10
FEATURE [Part::Box] Box003  label="Cube003"
  AttacherType = Attacher::AttachEngine3D
  Height = 10
  Length = 190
  Placement = pos=(-90,-50,-10) rot=(0,0,1;0rad)
  Width = 50
FEATURE [Sketcher::SketchObject] Sketch021
  FullyConstrained = true
  Placement = pos=(0,-14.3,2.37) rot=(-1,0,0;2.03453rad)
  sketch-geometry (6):
    g0: LineSegment StartX=41.65 StartY=-3.15 StartZ=0 EndX=38.95 EndY=-3.15 EndZ=0
    g1: LineSegment StartX=36.25 StartY=-3.15 StartZ=0 EndX=38.95 EndY=-3.15 EndZ=0
    g2: LineSegment StartX=41.65 StartY=-3.15 StartZ=0 EndX=41.65 EndY=-7.15 EndZ=0
    g3: LineSegment StartX=38.95 StartY=-7.15 StartZ=0 EndX=41.65 EndY=-7.15 EndZ=0
    g4: LineSegment StartX=38.95 StartY=-7.15 StartZ=0 EndX=36.25 EndY=-7.15 EndZ=0
    g5: LineSegment StartX=36.25 StartY=-3.15 StartZ=0 EndX=36.25 EndY=-7.15 EndZ=0
  constraints (16):
    c: Horizontal(g0)
    c: Distance(g0) = 2.7
    c: Horizontal(g1)
    c: Distance(g1) = 2.7
    c: Coincident(g1,g0)
    c: Block(g0)
    c: Coincident(g2,g0)
    c: Vertical(g2)
    c: Horizontal(g3)
    c: Coincident(g3,g2)
    c: Horizontal(g4)
    c: Coincident(g5,g1)
    c: Vertical(g5)
    c: Coincident(g5,g4)
    c: Block(g3)
    c: Block(g4)
FEATURE [Sketcher::SketchObject] Sketch022
  FullyConstrained = true
  Placement = pos=(0,-14.3,2.37) rot=(-1,0,0;2.03453rad)
  sketch-geometry (6):
    g0: LineSegment StartX=41.65 StartY=-3.15 StartZ=0 EndX=38.95 EndY=-3.15 EndZ=0
    g1: LineSegment StartX=36.25 StartY=-3.15 StartZ=0 EndX=38.95 EndY=-3.15 EndZ=0
    g2: LineSegment StartX=41.65 StartY=-3.15 StartZ=0 EndX=41.65 EndY=-7.15 EndZ=0
    g3: LineSegment StartX=38.95 StartY=-7.15 StartZ=0 EndX=41.65 EndY=-7.15 EndZ=0
    g4: LineSegment StartX=38.95 StartY=-7.15 StartZ=0 EndX=36.25 EndY=-7.15 EndZ=0
    g5: LineSegment StartX=36.25 StartY=-3.15 StartZ=0 EndX=36.25 EndY=-7.15 EndZ=0
  constraints (16):
    c: Horizontal(g0)
    c: Distance(g0) = 2.7
    c: Horizontal(g1)
    c: Distance(g1) = 2.7
    c: Coincident(g1,g0)
    c: Block(g0)
    c: Coincident(g2,g0)
    c: Vertical(g2)
    c: Horizontal(g3)
    c: Coincident(g3,g2)
    c: Horizontal(g4)
    c: Coincident(g5,g1)
    c: Vertical(g5)
    c: Coincident(g5,g4)
    c: Block(g3)
    c: Block(g4)
FEATURE [Sketcher::SketchObject] Sketch024
  FullyConstrained = true
  Placement = pos=(0,-14.3,2.37) rot=(-1,0,0;2.03453rad)
  sketch-geometry (4):
    g0: LineSegment StartX=49.5 StartY=-21.2 StartZ=0 EndX=49.5 EndY=-22.8 EndZ=0
    g1: LineSegment StartX=49.5 StartY=-22.8 StartZ=0 EndX=0.002238 EndY=-22.8 EndZ=0
    g2: LineSegment StartX=0.002238 StartY=-21.2 StartZ=0 EndX=0.002238 EndY=-22.8 EndZ=0
    g3: LineSegment StartX=49.5 StartY=-21.2 StartZ=0 EndX=0.002238 EndY=-21.2 EndZ=0
  constraints (10):
    c: Vertical(g0)
    c: Distance(g0) = 1.6
    c: Coincident(g1,g0)
    c: Horizontal(g1)
    c: Vertical(g2)
    c: Coincident(g2,g1)
    c: Coincident(g3,g0)
    c: Coincident(g3,g2)
    c: Horizontal(g3)
    c: Block(g3)
FEATURE [Sketcher::SketchObject] Sketch025
  FullyConstrained = true
  Placement = pos=(0,-14.3,2.37) rot=(-1,0,0;2.03453rad)
  sketch-geometry (4):
    g0: LineSegment StartX=0 StartY=1.5 StartZ=0 EndX=0 EndY=0 EndZ=0
    g1: LineSegment StartX=0 StartY=1.5 StartZ=0 EndX=5 EndY=1.5 EndZ=0
    g2: LineSegment StartX=5 StartY=1.5 StartZ=0 EndX=5 EndY=0 EndZ=0
    g3: LineSegment StartX=0 StartY=0 StartZ=0 EndX=5 EndY=0 EndZ=0
  constraints (13):
    c: Vertical(g0)
    c: Distance(g0) = 1.5
    c: Horizontal(g1)
    c: Distance(g1) = 5
    c: Coincident(g1,g0)
    c: Vertical(g2)
    c: Distance(g2) = 1.5
    c: Coincident(g2,g1)
    c: Block(g1)
    c: Block(g2)
    c: Block(g0)
    c: Coincident(g3,g0)
    c: Coincident(g3,g2)
FEATURE [Part::Extrusion] Extrude022  label="solenoidDriverBottomLipTopExtrude014"
  Base = -> Sketch025
  Dir = (0,0.894389,-0.447291)
  DirMode = 2
  FaceMakerClass = Part::FaceMakerBullseye
  LengthFwd = -6.5
  LengthRev = 0
  Placement = pos=(0,-15.45,20.3) rot=(1,0,0;1.5708rad)
  Solid = true
  Symmetric = false
FEATURE [Part::Fillet] Fillet013  label="solenoidDriverBottomLipTopFillet006"
  Base = -> Extrude022
  Edges = 1 edges r=1.4: [Edge6]
  Placement = pos=(5,0,0) rot=(0,0,1;0rad)
FEATURE [Sketcher::SketchObject] Sketch026
  FullyConstrained = true
  Placement = pos=(0,-14.3,2.37) rot=(-1,0,0;2.03453rad)
  sketch-geometry (4):
    g0: LineSegment StartX=0 StartY=1.5 StartZ=0 EndX=0 EndY=0 EndZ=0
    g1: LineSegment StartX=0 StartY=1.5 StartZ=0 EndX=5 EndY=1.5 EndZ=0
    g2: LineSegment StartX=5 StartY=1.5 StartZ=0 EndX=5 EndY=0 EndZ=0
    g3: LineSegment StartX=0 StartY=0 StartZ=0 EndX=5 EndY=0 EndZ=0
  constraints (13):
    c: Vertical(g0)
    c: Distance(g0) = 1.5
    c: Horizontal(g1)
    c: Distance(g1) = 5
    c: Coincident(g1,g0)
    c: Vertical(g2)
    c: Distance(g2) = 1.5
    c: Coincident(g2,g1)
    c: Block(g1)
    c: Block(g2)
    c: Block(g0)
    c: Coincident(g3,g0)
    c: Coincident(g3,g2)
FEATURE [Part::Extrusion] Extrude023  label="solenoidDriverBottomLipTopExtrude015"
  Base = -> Sketch026
  Dir = (0,0.894389,-0.447291)
  DirMode = 2
  FaceMakerClass = Part::FaceMakerBullseye
  LengthFwd = -6.5
  LengthRev = 0
  Placement = pos=(5,-14.15,19.65) rot=(1,0,0;1.5708rad)
  Solid = true
  Symmetric = false
FEATURE [Sketcher::SketchObject] Sketch027
  FullyConstrained = true
  Placement = pos=(0,-14.3,2.37) rot=(-1,0,0;2.03453rad)
  sketch-geometry (5):
    g0: LineSegment StartX=45.5 StartY=-21.2 StartZ=0 EndX=49.5 EndY=-21.2 EndZ=0
    g1: LineSegment StartX=49.5 StartY=0 StartZ=0 EndX=49.5 EndY=-21.2 EndZ=0
    g2: LineSegment StartX=49.5 StartY=0 StartZ=0 EndX=49.5 EndY=1.6 EndZ=0
    g3: LineSegment StartX=45.5 StartY=-21.2 StartZ=0 EndX=45.5 EndY=1.6 EndZ=0
    g4: LineSegment StartX=49.5 StartY=1.6 StartZ=0 EndX=45.5 EndY=1.6 EndZ=0
  constraints (14):
    c: Horizontal(g0)
    c: Distance(g0) = 4
    c: Coincident(g1,g0)
    c: Vertical(g1)
    c: Block(g1)
    c: Vertical(g2)
    c: Distance(g2) = 1.6
    c: Block(g2)
    c: Coincident(g3,g0)
    c: Vertical(g3)
    c: Coincident(g4,g2)
    c: Horizontal(g4)
    c: Block(g0)
    c: Coincident(g3,g4)
FEATURE [Part::Extrusion] Extrude024
  Base = -> Sketch027
  Dir = (0,0.894389,-0.447291)
  DirMode = 2
  FaceMakerClass = Part::FaceMakerBullseye
  LengthFwd = 6.34
  LengthRev = 0
  Placement = pos=(0,-5.59,1) rot=(0,0,1;0rad)
  Solid = true
  Symmetric = false
FEATURE [Part::Fillet] Fillet014  label="solenoidDriverSideBarFillet014"
  Base = -> Extrude024
  Edges = 1 edges r=1.4: [Edge14]
  Placement = pos=(0,0.9,-0.45) rot=(0,0,1;0rad)
FEATURE [Part::Revolution] Revolve  label="mainScrewStandRevolve"
  Angle = 360
  Axis = (0,0,1)
  Base = (0,0,0)
  FaceMakerClass = Part::FaceMakerBullseye
  Placement = pos=(121.35,-15.3,0) rot=(0,0,1;0rad)
  Solid = true
  Source = -> Sketch004
  Symmetric = false
FEATURE [Part::Extrusion] Extrude021  label="solenoidDriverTopLipLowerExtrude011"
  Base = -> Sketch024
  Dir = (0,0.894389,-0.447291)
  DirMode = 2
  FaceMakerClass = Part::FaceMakerBullseye
  LengthFwd = 5.05
  LengthRev = 0
  Solid = true
  Symmetric = false
FEATURE [Part::Fillet] Fillet012  label="solenoidDriverTopLipLowerFillet004"
  Base = -> Extrude021
  Edges = 1 edges r=1.2: [Edge7]
  Placement = pos=(0,-0.9,-1.35) rot=(0,0,1;0rad)
FEATURE [Part::Fillet] Fillet003  label="solenoidDriverTopLipLowerFillet003"
  Base = -> Extrude010
  Edges = 1 edges r=1.2: [Edge7]
  Placement = pos=(0,-3,-0.3) rot=(0,0,1;0rad)
FEATURE [Part::Extrusion] Extrude025  label="mainBodyUpperExtrude025"
  Base = -> Sketch001
  Dir = (0,0,1)
  DirMode = 2
  FaceMakerClass = Part::FaceMakerBullseye
  LengthFwd = 20
  LengthRev = 0
  Solid = true
  Symmetric = false
FEATURE [Part::MultiFuse] Fusion  label="solenoidDriverBottomLipFusion"
  Placement = pos=(0,-1.6,0) rot=(0,0,1;0rad)
  Shapes = -> [Fillet005,Fillet013,Extrude023,Extrude013]
FEATURE [Sketcher::SketchObject] Sketch028
  FullyConstrained = true
  Placement = pos=(0,-14.3,2.37) rot=(-1,0,0;2.03453rad)
  sketch-geometry (4):
    g0: LineSegment StartX=0 StartY=1.5 StartZ=0 EndX=0 EndY=0 EndZ=0
    g1: LineSegment StartX=0 StartY=1.5 StartZ=0 EndX=5 EndY=1.5 EndZ=0
    g2: LineSegment StartX=5 StartY=1.5 StartZ=0 EndX=5 EndY=0 EndZ=0
    g3: LineSegment StartX=0 StartY=0 StartZ=0 EndX=5 EndY=0 EndZ=0
  constraints (13):
    c: Vertical(g0)
    c: Distance(g0) = 1.5
    c: Horizontal(g1)
    c: Distance(g1) = 5
    c: Coincident(g1,g0)
    c: Vertical(g2)
    c: Distance(g2) = 1.5
    c: Coincident(g2,g1)
    c: Block(g1)
    c: Block(g2)
    c: Block(g0)
    c: Coincident(g3,g0)
    c: Coincident(g3,g2)
FEATURE [Part::Extrusion] Extrude026  label="solenoidDriverBottomLipTopExtrude016"
  Base = -> Sketch028
  Dir = (0,0.894389,-0.447291)
  DirMode = 2
  FaceMakerClass = Part::FaceMakerBullseye
  LengthFwd = -6.5
  LengthRev = 0
  Placement = pos=(5,-14.15,19.65) rot=(1,0,0;1.5708rad)
  Solid = true
  Symmetric = false
FEATURE [Sketcher::SketchObject] Sketch029
  FullyConstrained = true
  Placement = pos=(0,-14.3,2.37) rot=(-1,0,0;2.03453rad)
  sketch-geometry (4):
    g0: LineSegment StartX=0 StartY=1.5 StartZ=0 EndX=0 EndY=0 EndZ=0
    g1: LineSegment StartX=0 StartY=1.5 StartZ=0 EndX=5 EndY=1.5 EndZ=0
    g2: LineSegment StartX=5 StartY=1.5 StartZ=0 EndX=5 EndY=0 EndZ=0
    g3: LineSegment StartX=0 StartY=0 StartZ=0 EndX=5 EndY=0 EndZ=0
  constraints (13):
    c: Vertical(g0)
    c: Distance(g0) = 1.5
    c: Horizontal(g1)
    c: Distance(g1) = 5
    c: Coincident(g1,g0)
    c: Vertical(g2)
    c: Distance(g2) = 1.5
    c: Coincident(g2,g1)
    c: Block(g1)
    c: Block(g2)
    c: Block(g0)
    c: Coincident(g3,g0)
    c: Coincident(g3,g2)
FEATURE [Part::Extrusion] Extrude027  label="solenoidDriverBottomLipTopExtrude017"
  Base = -> Sketch029
  Dir = (0,0.894389,-0.447291)
  DirMode = 2
  FaceMakerClass = Part::FaceMakerBullseye
  LengthFwd = -6.5
  LengthRev = 0
  Placement = pos=(0,-14.15,19.65) rot=(1,0,0;1.5708rad)
  Solid = true
  Symmetric = false
FEATURE [Sketcher::SketchObject] Sketch030
  FullyConstrained = true
  Placement = pos=(0,-14.3,2.37) rot=(-1,0,0;2.03453rad)
  sketch-geometry (4):
    g0: LineSegment StartX=0 StartY=1.5 StartZ=0 EndX=0 EndY=0 EndZ=0
    g1: LineSegment StartX=0 StartY=1.5 StartZ=0 EndX=5 EndY=1.5 EndZ=0
    g2: LineSegment StartX=5 StartY=1.5 StartZ=0 EndX=5 EndY=0 EndZ=0
    g3: LineSegment StartX=0 StartY=0 StartZ=0 EndX=5 EndY=0 EndZ=0
  constraints (13):
    c: Vertical(g0)
    c: Distance(g0) = 1.5
    c: Horizontal(g1)
    c: Distance(g1) = 5
    c: Coincident(g1,g0)
    c: Vertical(g2)
    c: Distance(g2) = 1.5
    c: Coincident(g2,g1)
    c: Block(g1)
    c: Block(g2)
    c: Block(g0)
    c: Coincident(g3,g0)
    c: Coincident(g3,g2)
FEATURE [Sketcher::SketchObject] Sketch031
  FullyConstrained = true
  Placement = pos=(0,-14.3,2.37) rot=(-1,0,0;2.03453rad)
  sketch-geometry (6):
    g0: LineSegment StartX=45.5 StartY=-21.2 StartZ=0 EndX=49.5 EndY=-21.2 EndZ=0
    g1: LineSegment StartX=45.5 StartY=0 StartZ=0 EndX=49.5 EndY=0 EndZ=0
    g2: LineSegment StartX=49.5 StartY=0 StartZ=0 EndX=49.5 EndY=-21.2 EndZ=0
    g3: LineSegment StartX=4 StartY=0 StartZ=0 EndX=4 EndY=-21.2 EndZ=0
    g4: LineSegment StartX=45.5 StartY=-21.2 StartZ=0 EndX=4 EndY=-21.2 EndZ=0
    g5: LineSegment StartX=4 StartY=0 StartZ=0 EndX=45.5 EndY=0 EndZ=0
  constraints (16):
    c: Horizontal(g0)
    c: Distance(g0) = 4
    c: Horizontal(g1)
    c: Distance(g1) = 4
    c: Coincident(g2,g1)
    c: Coincident(g2,g0)
    c: Vertical(g2)
    c: Block(g2)
    c: Vertical(g3)
    c: Coincident(g4,g0)
    c: Horizontal(g4)
    c: Coincident(g4,g3)
    c: Coincident(g5,g1)
    c: Horizontal(g5)
    c: Block(g3)
    c: Block(g5)
FEATURE [Part::Extrusion] Extrude028  label="removeFromSolenoidDriverMainExtrude021"
  Base = -> Sketch031
  Dir = (0,0.894389,-0.447291)
  DirMode = 2
  FaceMakerClass = Part::FaceMakerBullseye
  LengthFwd = 3.1
  LengthRev = 0
  Placement = pos=(-4,-2.42,-0.8) rot=(0,0,1;0rad)
  Solid = true
  Symmetric = false
FEATURE [Part::Extrusion] Extrude029  label="solenoidDriverBottomLipTopExtrude018"
  Base = -> Sketch030
  Dir = (0,0.894389,-0.447291)
  DirMode = 2
  FaceMakerClass = Part::FaceMakerBullseye
  LengthFwd = -6.5
  LengthRev = 0
  Placement = pos=(5,-14.15,19.65) rot=(1,0,0;1.5708rad)
  Solid = true
  Symmetric = false
FEATURE [Sketcher::SketchObject] Sketch032
  FullyConstrained = true
  Placement = pos=(0,-14.3,2.37) rot=(-1,0,0;2.03453rad)
  sketch-geometry (4):
    g0: LineSegment StartX=0 StartY=1.5 StartZ=0 EndX=0 EndY=0 EndZ=0
    g1: LineSegment StartX=0 StartY=1.5 StartZ=0 EndX=5 EndY=1.5 EndZ=0
    g2: LineSegment StartX=5 StartY=1.5 StartZ=0 EndX=5 EndY=0 EndZ=0
    g3: LineSegment StartX=0 StartY=0 StartZ=0 EndX=5 EndY=0 EndZ=0
  constraints (13):
    c: Vertical(g0)
    c: Distance(g0) = 1.5
    c: Horizontal(g1)
    c: Distance(g1) = 5
    c: Coincident(g1,g0)
    c: Vertical(g2)
    c: Distance(g2) = 1.5
    c: Coincident(g2,g1)
    c: Block(g1)
    c: Block(g2)
    c: Block(g0)
    c: Coincident(g3,g0)
    c: Coincident(g3,g2)
FEATURE [Part::Extrusion] Extrude030  label="solenoidDriverBottomLipTopExtrude019"
  Base = -> Sketch032
  Dir = (0,0.894389,-0.447291)
  DirMode = 2
  FaceMakerClass = Part::FaceMakerBullseye
  LengthFwd = -6.5
  LengthRev = 0
  Placement = pos=(0,-14.15,19.65) rot=(1,0,0;1.5708rad)
  Solid = true
  Symmetric = false
FEATURE [Part::MultiFuse] Fusion004
  Placement = pos=(0,1.4,2.65) rot=(0,0,1;0rad)
  Shapes = -> [Extrude029,Extrude030]
FEATURE [Part::MultiFuse] Fusion003
  Placement = pos=(-2.3,0,0) rot=(0,0,1;0rad)
  Shapes = -> [Extrude028,Fusion004]
FEATURE [Sketcher::SketchObject] Sketch033
  FullyConstrained = true
  Placement = pos=(0,-14.3,2.37) rot=(-1,0,0;2.03453rad)
  sketch-geometry (4):
    g0: LineSegment StartX=0 StartY=1.5 StartZ=0 EndX=0 EndY=0 EndZ=0
    g1: LineSegment StartX=0 StartY=1.5 StartZ=0 EndX=5 EndY=1.5 EndZ=0
    g2: LineSegment StartX=5 StartY=1.5 StartZ=0 EndX=5 EndY=0 EndZ=0
    g3: LineSegment StartX=0 StartY=0 StartZ=0 EndX=5 EndY=0 EndZ=0
  constraints (13):
    c: Vertical(g0)
    c: Distance(g0) = 1.5
    c: Horizontal(g1)
    c: Distance(g1) = 5
    c: Coincident(g1,g0)
    c: Vertical(g2)
    c: Distance(g2) = 1.5
    c: Coincident(g2,g1)
    c: Block(g1)
    c: Block(g2)
    c: Block(g0)
    c: Coincident(g3,g0)
    c: Coincident(g3,g2)
FEATURE [Sketcher::SketchObject] Sketch034
  FullyConstrained = true
  Placement = pos=(0,-14.3,2.37) rot=(-1,0,0;2.03453rad)
  sketch-geometry (4):
    g0: LineSegment StartX=0 StartY=1.5 StartZ=0 EndX=4 EndY=1.5 EndZ=0
    g1: LineSegment StartX=4 StartY=1.5 StartZ=0 EndX=4 EndY=-2.5 EndZ=0
    g2: LineSegment StartX=4 StartY=-2.5 StartZ=0 EndX=0 EndY=-2.5 EndZ=0
    g3: LineSegment StartX=0 StartY=1.5 StartZ=0 EndX=0 EndY=-2.5 EndZ=0
  constraints (11):
    c: Horizontal(g0)
    c: Distance(g0) = 4
    c: Block(g0)
    c: Coincident(g1,g0)
    c: Vertical(g1)
    c: Distance(g1) = 4
    c: Coincident(g2,g1)
    c: Horizontal(g2)
    c: Distance(g2) = 4
    c: Coincident(g3,g0)
    c: Coincident(g3,g2)
FEATURE [Part::Extrusion] Extrude020  label="removeFromSolenoidDriverMainExtrude020"
  Base = -> Sketch020
  Dir = (0,0.894389,-0.447291)
  DirMode = 2
  FaceMakerClass = Part::FaceMakerBullseye
  LengthFwd = 3.1
  LengthRev = 0
  Placement = pos=(-4,-2.42,-0.8) rot=(0,0,1;0rad)
  Solid = true
  Symmetric = false
FEATURE [Part::Fillet] Fillet
  Base = -> Fusion003
  Edges = 1 edges r=10: [Edge5]
  Placement = pos=(-2,0,0) rot=(0,0,1;0rad)
FEATURE [Part::MultiFuse] Fusion001
  Placement = pos=(0,1.4,2.65) rot=(0,0,1;0rad)
  Shapes = -> [Extrude026,Extrude027]
FEATURE [Part::MultiFuse] Fusion002
  Shapes = -> [Extrude020,Fusion001]
FEATURE [Sketcher::SketchObject] Sketch035
  FullyConstrained = true
  Placement = pos=(0,-14.3,2.37) rot=(-1,0,0;2.03453rad)
  sketch-geometry (4):
    g0: LineSegment StartX=0 StartY=1.5 StartZ=0 EndX=0 EndY=0 EndZ=0
    g1: LineSegment StartX=0 StartY=1.5 StartZ=0 EndX=5 EndY=1.5 EndZ=0
    g2: LineSegment StartX=5 StartY=1.5 StartZ=0 EndX=5 EndY=0 EndZ=0
    g3: LineSegment StartX=0 StartY=0 StartZ=0 EndX=5 EndY=0 EndZ=0
  constraints (13):
    c: Vertical(g0)
    c: Distance(g0) = 1.5
    c: Horizontal(g1)
    c: Distance(g1) = 5
    c: Coincident(g1,g0)
    c: Vertical(g2)
    c: Distance(g2) = 1.5
    c: Coincident(g2,g1)
    c: Block(g1)
    c: Block(g2)
    c: Block(g0)
    c: Coincident(g3,g0)
    c: Coincident(g3,g2)
FEATURE [Sketcher::SketchObject] Sketch036
  FullyConstrained = true
  Placement = pos=(0,-14.3,2.37) rot=(-1,0,0;2.03453rad)
  sketch-geometry (4):
    g0: LineSegment StartX=0 StartY=1.5 StartZ=0 EndX=0 EndY=0 EndZ=0
    g1: LineSegment StartX=0 StartY=1.5 StartZ=0 EndX=5 EndY=1.5 EndZ=0
    g2: LineSegment StartX=5 StartY=1.5 StartZ=0 EndX=5 EndY=0 EndZ=0
    g3: LineSegment StartX=0 StartY=0 StartZ=0 EndX=5 EndY=0 EndZ=0
  constraints (13):
    c: Vertical(g0)
    c: Distance(g0) = 1.5
    c: Horizontal(g1)
    c: Distance(g1) = 5
    c: Coincident(g1,g0)
    c: Vertical(g2)
    c: Distance(g2) = 1.5
    c: Coincident(g2,g1)
    c: Block(g1)
    c: Block(g2)
    c: Block(g0)
    c: Coincident(g3,g0)
    c: Coincident(g3,g2)
FEATURE [Part::Extrusion] Extrude031  label="solenoidDriverBottomLipTopExtrude020"
  Base = -> Sketch035
  Dir = (0,0.894389,-0.447291)
  DirMode = 2
  FaceMakerClass = Part::FaceMakerBullseye
  LengthFwd = -6.5
  LengthRev = 0
  Placement = pos=(5,-14.15,19.65) rot=(1,0,0;1.5708rad)
  Solid = true
  Symmetric = false
FEATURE [Part::Extrusion] Extrude032  label="solenoidDriverBottomLipTopExtrude021"
  Base = -> Sketch036
  Dir = (0,0.894389,-0.447291)
  DirMode = 2
  FaceMakerClass = Part::FaceMakerBullseye
  LengthFwd = -6.5
  LengthRev = 0
  Placement = pos=(0,-14.15,19.65) rot=(1,0,0;1.5708rad)
  Solid = true
  Symmetric = false
FEATURE [Part::MultiFuse] Fusion009
  Placement = pos=(8,1.4,2.65) rot=(0,0,1;0rad)
  Shapes = -> [Extrude031,Extrude032]
FEATURE [Part::MultiFuse] Fusion010  label="removeFromSolenoidDriver"
  Shapes = -> [Fusion009,Fillet,Fusion002]
FEATURE [Sketcher::SketchObject] Sketch037
  FullyConstrained = true
  Placement = pos=(0,0,0) rot=(1,0,0;1.5708rad)
  sketch-geometry (4):
    g0: Circle CenterX=64.05 CenterY=16.5 CenterZ=0 NormalX=0 NormalY=0 NormalZ=1 AngleXU=0 Radius=2.7
    g1: Circle CenterX=64.05 CenterY=8.5 CenterZ=0 NormalX=0 NormalY=0 NormalZ=1 AngleXU=0 Radius=2.7
    g2: Circle CenterX=84.15 CenterY=8.5 CenterZ=0 NormalX=0 NormalY=0 NormalZ=1 AngleXU=0 Radius=2.7
    g3: Circle CenterX=84.15 CenterY=16.5 CenterZ=0 NormalX=0 NormalY=0 NormalZ=1 AngleXU=0 Radius=2.7
  constraints (4):
    c: Block(g2)
    c: Block(g3)
    c: Block(g0)
    c: Block(g1)
FEATURE [Part::Extrusion] Extrude033  label="removeFromMainBodyToCreateScrewHoleCounterSinks001"
  Base = -> Sketch037
  Dir = (0,-1,1.1e-15)
  DirMode = 2
  FaceMakerClass = Part::FaceMakerBullseye
  LengthFwd = 1.9
  LengthRev = 0
  Placement = pos=(0.8,0,0) rot=(0,0,1;0rad)
  Solid = true
  Symmetric = false
FEATURE [Part::MultiFuse] Fusion011  label="removeFromMainBodyToCreateScrewHoleCounterSinks001Fusion011"
  Shapes = -> [Extrude014,Extrude033]
FEATURE [Sketcher::SketchObject] Sketch038
  FullyConstrained = true
  Placement = pos=(0,-14.3,2.37) rot=(-1,0,0;2.03453rad)
  sketch-geometry (4):
    g0: LineSegment StartX=33.9 StartY=-9.7 StartZ=0 EndX=33.9 EndY=-1.5 EndZ=0
    g1: LineSegment StartX=33.9 StartY=-1.5 StartZ=0 EndX=44.5 EndY=-1.5 EndZ=0
    g2: LineSegment StartX=33.9 StartY=-9.7 StartZ=0 EndX=44.5 EndY=-9.7 EndZ=0
    g3: LineSegment StartX=44.5 StartY=-1.5 StartZ=0 EndX=44.5 EndY=-9.7 EndZ=0
  constraints (10):
    c: Vertical(g0)
    c: Coincident(g1,g0)
    c: Horizontal(g1)
    c: Block(g1)
    c: Block(g0)
    c: Coincident(g2,g0)
    c: Horizontal(g2)
    c: Coincident(g3,g1)
    c: Coincident(g3,g2)
    c: Vertical(g3)
FEATURE [Part::Extrusion] Extrude034
  Base = -> Sketch038
  Dir = (0,0.894389,-0.447291)
  DirMode = 2
  FaceMakerClass = Part::FaceMakerBullseye
  LengthFwd = 16
  LengthRev = 0
  Placement = pos=(0,-22,7) rot=(0,0,1;0rad)
  Solid = true
  Symmetric = false
FEATURE [Sketcher::SketchObject] Sketch039
  FullyConstrained = true
  Placement = pos=(0,-14.3,2.37) rot=(-1,0,0;2.03453rad)
  sketch-geometry (4):
    g0: LineSegment StartX=5.5 StartY=-7.7 StartZ=0 EndX=13.3 EndY=-7.7 EndZ=0
    g1: LineSegment StartX=13.3 StartY=-7.7 StartZ=0 EndX=13.3 EndY=-13.1 EndZ=0
    g2: LineSegment StartX=13.3 StartY=-13.1 StartZ=0 EndX=5.5 EndY=-13.1 EndZ=0
    g3: LineSegment StartX=5.5 StartY=-7.7 StartZ=0 EndX=5.5 EndY=-13.1 EndZ=0
  constraints (12):
    c: Horizontal(g0)
    c: Distance(g0) = 7.8
    c: Coincident(g1,g0)
    c: Vertical(g1)
    c: Distance(g1) = 5.4
    c: Coincident(g2,g1)
    c: Horizontal(g2)
    c: Vertical(g3)
    c: Coincident(g3,g2)
    c: Block(g0)
    c: Block(g2)
    c: Block(g3)
FEATURE [Part::Extrusion] Extrude035  label="removeToMakeHoleForConnectorExtrude035"
  Base = -> Sketch039
  Dir = (0,0.894389,-0.447291)
  DirMode = 2
  FaceMakerClass = Part::FaceMakerBullseye
  LengthFwd = 15
  LengthRev = 0
  Placement = pos=(-4,-22,9.6469) rot=(0,0,1;0rad)
  Solid = true
  Symmetric = false
FEATURE [App::MeasureDistance] Distance  label="Distance: 4.00 mm"
  Distance = 4.00184
  P1 = (119.349,-15.3,8)
  P2 = (123.351,-15.3,8)
FEATURE [App::MeasureDistance] Distance001  label="Distance: 3.80 mm"
  Distance = 3.8
  P1 = (119.45,-15.3,8)
  P2 = (123.25,-15.3,8)
FEATURE [Part::Fillet] Fillet015
  Base = -> Extrude009
  Edges = 1 edges r=1.59: [Edge7]
FEATURE [Part::Fillet] Fillet016
  Base = -> Extrude017
  Edges = 1 edges r=1.49: [Edge12]
FEATURE [Part::Fillet] Fillet017
  Base = -> Fillet016
  Edges = 1 edges r=1.45: [Edge8]
FEATURE [Part::MultiFuse] Fusion012  label="main"
  Shapes = -> [Extrude,Revolve,Extrude005,Fillet003,Fillet012,Fillet014,Extrude025,Fusion,Fillet015,Fillet017]
FEATURE [Part::Cut] Cut001
  Base = -> Fusion012
  Tool = -> Box003
FEATURE [Part::Cut] Cut002
  Base = -> Cut001
  Tool = -> Box002
FEATURE [Part::Cut] Cut003
  Base = -> Cut002
  Tool = -> Cut
FEATURE [Part::Cut] Cut004
  Base = -> Cut003
  Tool = -> Extrude019
FEATURE [Part::Cut] Cut005
  Base = -> Cut004
  Tool = -> Fusion011
FEATURE [Part::Cut] Cut006
  Base = -> Cut005
  Tool = -> Extrude004
FEATURE [Part::Cut] Cut007
  Base = -> Cut006
  Tool = -> Extrude015
FEATURE [Part::Cut] Cut008
  Base = -> Cut007
  Tool = -> Extrude008
FEATURE [Part::Cut] Cut009
  Base = -> Cut008
  Tool = -> Fusion010
FEATURE [App::MeasureDistance] Distance002  label="Distance: 2.05 mm"
  Distance = 2.05453
  P1 = (1.5,-23.0732,21.402)
  P2 = (6e-15,-23,20)
FEATURE [Part::Cut] Cut010
  Base = -> Cut009
  Tool = -> Extrude035
FEATURE [Part::Cut] Cut011
  Base = -> Cut010
  Tool = -> Extrude034
FEATURE [Part::Box] Box004  label="Cube004"
  AttacherType = Attacher::AttachEngine3D
  Height = 10
  Length = 200
  Placement = pos=(-30,0,0) rot=(0,0,1;0rad)
  Width = 10
FEATURE [Part::Fillet] Fillet020
  Base = -> Box004
  Edges = 1 edges r=3.6: [Edge12]
FEATURE [Part::Box] Box005  label="Cube005"
  AttacherType = Attacher::AttachEngine3D
  Height = 10
  Length = 198
  Placement = pos=(-30,0,0) rot=(0,0,1;0rad)
  Width = 10
FEATURE [Part::Cut] Cut012
  Base = -> Box005
  Tool = -> Fillet020
FEATURE [Part::Box] Box006  label="Cube006"
  AttacherType = Attacher::AttachEngine3D
  Height = 5
  Length = 200
  Placement = pos=(-30,6.4,10) rot=(1,0,0;0rad)
  Width = 5
FEATURE [Part::Box] Box007  label="Cube007"
  AttacherType = Attacher::AttachEngine3D
  Height = 5
  Length = 200
  Placement = pos=(-30,6.4,10) rot=(1,0,0;0.872665rad)
  Width = 5
FEATURE [Part::MultiFuse] Fusion013  label="removeFromMainFusion013"
  Placement = pos=(0,-10,10) rot=(0,0,1;0rad)
  Shapes = -> [Box007,Box006,Cut012]
FEATURE [Mesh::Feature] v0_98_Cut013  label="v0_98-Cut013"
FEATURE [App::MeasureDistance] Distance003  label="Distance: 7.18 mm"
  Distance = 7.17719
  P1 = (117.773,-15.3145,-2.4)
  P2 = (124.951,-15.2973,-2.4)
FEATURE [Sketcher::SketchObject] Sketch040
  FullyConstrained = true
  Placement = pos=(0,-14.3,2.37) rot=(-1,0,0;2.03453rad)
  sketch-geometry (4):
    g0: LineSegment StartX=0 StartY=1.5 StartZ=0 EndX=0 EndY=0 EndZ=0
    g1: LineSegment StartX=0 StartY=1.5 StartZ=0 EndX=5 EndY=1.5 EndZ=0
    g2: LineSegment StartX=5 StartY=1.5 StartZ=0 EndX=5 EndY=0 EndZ=0
    g3: LineSegment StartX=0 StartY=0 StartZ=0 EndX=5 EndY=0 EndZ=0
  constraints (13):
    c: Vertical(g0)
    c: Distance(g0) = 1.5
    c: Horizontal(g1)
    c: Distance(g1) = 5
    c: Coincident(g1,g0)
    c: Vertical(g2)
    c: Distance(g2) = 1.5
    c: Coincident(g2,g1)
    c: Block(g1)
    c: Block(g2)
    c: Block(g0)
    c: Coincident(g3,g0)
    c: Coincident(g3,g2)
FEATURE [Part::Extrusion] Extrude036
  Base = -> Sketch040
  Dir = (0,0.894389,-0.447291)
  DirMode = 2
  FaceMakerClass = Part::FaceMakerBullseye
  LengthFwd = 1.4
  LengthRev = 0
  Placement = pos=(0,8.25,17.58) rot=(0,0,1;0rad)
  Solid = true
  Symmetric = false
FEATURE [Sketcher::SketchObject] Sketch041
  FullyConstrained = true
  Placement = pos=(0,-14.3,2.37) rot=(-1,0,0;2.03453rad)
  sketch-geometry (4):
    g0: LineSegment StartX=0 StartY=1.5 StartZ=0 EndX=0 EndY=0 EndZ=0
    g1: LineSegment StartX=0 StartY=1.5 StartZ=0 EndX=5 EndY=1.5 EndZ=0
    g2: LineSegment StartX=5 StartY=1.5 StartZ=0 EndX=5 EndY=0 EndZ=0
    g3: LineSegment StartX=0 StartY=0 StartZ=0 EndX=5 EndY=0 EndZ=0
  constraints (13):
    c: Vertical(g0)
    c: Distance(g0) = 1.5
    c: Horizontal(g1)
    c: Distance(g1) = 5
    c: Coincident(g1,g0)
    c: Vertical(g2)
    c: Distance(g2) = 1.5
    c: Coincident(g2,g1)
    c: Block(g1)
    c: Block(g2)
    c: Block(g0)
    c: Coincident(g3,g0)
    c: Coincident(g3,g2)
FEATURE [Part::Extrusion] Extrude037
  Base = -> Sketch041
  Dir = (0,0.894389,-0.447291)
  DirMode = 2
  FaceMakerClass = Part::FaceMakerBullseye
  LengthFwd = 1.4
  LengthRev = 0
  Placement = pos=(0,6.11,13.33) rot=(0,0,1;0rad)
  Solid = true
  Symmetric = false
FEATURE [Part::MultiFuse] Fusion014  label="screwSpacerFusion014"
  Shapes = -> [Extrude037,Extrude036]
FEATURE [Sketcher::SketchObject] Sketch042
  FullyConstrained = true
  Placement = pos=(0,-14.3,2.37) rot=(-1,0,0;2.03453rad)
  sketch-geometry (4):
    g0: LineSegment StartX=0 StartY=1.5 StartZ=0 EndX=0 EndY=0 EndZ=0
    g1: LineSegment StartX=0 StartY=1.5 StartZ=0 EndX=5 EndY=1.5 EndZ=0
    g2: LineSegment StartX=5 StartY=1.5 StartZ=0 EndX=5 EndY=0 EndZ=0
    g3: LineSegment StartX=0 StartY=0 StartZ=0 EndX=5 EndY=0 EndZ=0
  constraints (13):
    c: Vertical(g0)
    c: Distance(g0) = 1.5
    c: Horizontal(g1)
    c: Distance(g1) = 5
    c: Coincident(g1,g0)
    c: Vertical(g2)
    c: Distance(g2) = 1.5
    c: Coincident(g2,g1)
    c: Block(g1)
    c: Block(g2)
    c: Block(g0)
    c: Coincident(g3,g0)
    c: Coincident(g3,g2)
FEATURE [Part::Extrusion] Extrude038
  Base = -> Sketch042
  Dir = (0,0.894389,-0.447291)
  DirMode = 2
  FaceMakerClass = Part::FaceMakerBullseye
  LengthFwd = 1.4
  LengthRev = 0
  Placement = pos=(0,8.459,18) rot=(0,0,1;0rad)
  Solid = true
  Symmetric = false
FEATURE [Part::MultiFuse] Fusion015  label="screwSpacerFusion014Fusion015"
  Placement = pos=(0,0.35,-0.18) rot=(0,0,1;0rad)
  Shapes = -> [Extrude038,Fusion014]
FEATURE [Part::Cylinder] Cylinder
  Angle = 360
  AttacherType = Attacher::AttachEngine3D
  Height = 10
  Placement = pos=(0,10,0) rot=(0,0,1;0rad)
  Radius = 1.5
FEATURE [Part::Cylinder] Cylinder001
  Angle = 360
  AttacherType = Attacher::AttachEngine3D
  Height = 10
  Placement = pos=(3,10,0) rot=(0,0,1;0rad)
  Radius = 1.5
FEATURE [Part::Box] Box008  label="Cube008"
  AttacherType = Attacher::AttachEngine3D
  Height = 10
  Length = 3
  Placement = pos=(0,8.5,0) rot=(0,0,1;0rad)
  Width = 3
FEATURE [Part::MultiFuse] Fusion016  label="holeForWireFusion016"
  Shapes = -> [Cylinder001,Box008,Cylinder]
FEATURE [Part::Box] Box009  label="Cube009"
  AttacherType = Attacher::AttachEngine3D
  Height = 10
  Length = 3
  Placement = pos=(0,8.5,0) rot=(0,0,1;0rad)
  Width = 3
FEATURE [Part::Cylinder] Cylinder002
  Angle = 360
  AttacherType = Attacher::AttachEngine3D
  Height = 10
  Placement = pos=(0,10,0) rot=(0,0,1;0rad)
  Radius = 1.5
FEATURE [Part::Cylinder] Cylinder003
  Angle = 360
  AttacherType = Attacher::AttachEngine3D
  Height = 10
  Placement = pos=(3,10,0) rot=(0,0,1;0rad)
  Radius = 1.5
FEATURE [Part::MultiFuse] Fusion017  label="holeForWireFusion017"
  Placement = pos=(0,0,10) rot=(0,0,1;0rad)
  Shapes = -> [Cylinder003,Box009,Cylinder002]
FEATURE [Part::MultiFuse] Fusion018  label="holeForWireFusion018"
  Placement = pos=(0,0,0) rot=(0,-1,0;1.5708rad)
  Shapes = -> [Fusion017,Fusion016]
FEATURE [Part::Box] Box010  label="Cube010"
  AttacherType = Attacher::AttachEngine3D
  Height = 0.1
  Length = 0.1
  Placement = pos=(-2,10,0) rot=(0,0.995037,0.099504;0rad)
  Width = 0.1
FEATURE [Part::MultiFuse] Fusion019
  Placement = pos=(0,10,0) rot=(1,0,0;1.5708rad)
  Shapes = -> [Box010,Fusion018]
FEATURE [Part::Box] Box011  label="Cube011"
  AttacherType = Attacher::AttachEngine3D
  Height = 0.1
  Length = 1.1
  Placement = pos=(-2,10,10) rot=(0,0.995037,0.099504;0rad)
  Width = 0.1
FEATURE [Part::MultiFuse] Fusion020
  Placement = pos=(0,0,0) rot=(0,1,0;0.349066rad)
  Shapes = -> [Box011,Fusion019]
FEATURE [Part::Box] Box012  label="Cube012"
  AttacherType = Attacher::AttachEngine3D
  Height = 0.1
  Length = 1.1
  Placement = pos=(-2,10,10) rot=(0,0.995037,0.099504;0rad)
  Width = 0.1
FEATURE [Part::MultiFuse] Fusion021
  Placement = pos=(0,30,0) rot=(0,0,1;3.63029rad)
  Shapes = -> [Box012,Fusion020]
FEATURE [Part::Box] Box013  label="Cube013"
  AttacherType = Attacher::AttachEngine3D
  Height = 0.1
  Length = 1.1
  Placement = pos=(2,19,10) rot=(0,0.995037,0.099504;0rad)
  Width = 0.1
FEATURE [Part::MultiFuse] Fusion022  label="holeForWire"
  Placement = pos=(15,-49.8,-8.2) rot=(0,0,1;0rad)
  Shapes = -> [Box013,Fusion021]
FEATURE [Part::Cut] Cut013
  Base = -> Cut011
  Tool = -> Fusion013
FEATURE [Part::Cut] Cut014
  Base = -> Cut013
  Tool = -> Fusion022
FEATURE [Sketcher::SketchObject] Sketch043
  FullyConstrained = true
  MapMode = 4
  Placement = pos=(0,0,0) rot=(0.57735,0.57735,0.57735;2.0944rad)
  Support = -> [Cut014]
  sketch-geometry (14):
    g0: LineSegment StartX=6.08745 StartY=-4.11588 StartZ=0 EndX=6.08745 EndY=-2.11589 EndZ=0
    g1: LineSegment StartX=3.58745 StartY=2.38411 StartZ=0 EndX=3.58745 EndY=4.38411 EndZ=0
    g2: LineSegment StartX=8.08745 StartY=1.38411 StartZ=0 EndX=8.08745 EndY=-1.11589 EndZ=0
    g3: ArcOfCircle CenterX=7.08745 CenterY=-1.11589 CenterZ=0 NormalX=0 NormalY=0 NormalZ=1 AngleXU=0 Radius=1 StartAngle=4.71239 EndAngle=6.28319
    g4: LineSegment StartX=6.08745 StartY=-2.11589 StartZ=0 EndX=7.08745 EndY=-2.11589 EndZ=0
    g5: LineSegment StartX=6.08745 StartY=-4.11588 StartZ=0 EndX=7.08745 EndY=-4.11588 EndZ=0
    g6: ArcOfCircle CenterX=7.08745 CenterY=-1.11589 CenterZ=0 NormalX=0 NormalY=0 NormalZ=1 AngleXU=0 Radius=3 StartAngle=4.71239 EndAngle=6.28319
    g7: ArcOfCircle CenterX=7.08745 CenterY=1.38411 CenterZ=0 NormalX=0 NormalY=0 NormalZ=1 AngleXU=0 Radius=1 StartAngle=5.35e-14 EndAngle=1.5708
    g8: LineSegment StartX=3.58745 StartY=4.38411 StartZ=0 EndX=7.08745 EndY=4.38411 EndZ=0
    g9: LineSegment StartX=10.0875 StartY=-1.11588 StartZ=0 EndX=10.0875 EndY=1.38411 EndZ=0
    g10: ArcOfCircle CenterX=7.08745 CenterY=1.38411 CenterZ=0 NormalX=0 NormalY=0 NormalZ=1 AngleXU=0 Radius=3 StartAngle=3.57e-14 EndAngle=1.5708
    g11: LineSegment StartX=3.58745 StartY=2.38411 StartZ=0 EndX=3.58745 EndY=1.38411 EndZ=0
    g12: ArcOfCircle CenterX=4.58745 CenterY=1.38412 CenterZ=0 NormalX=0 NormalY=0 NormalZ=1 AngleXU=0 Radius=1 StartAngle=1.57081 EndAngle=3.14159
    g13: LineSegment StartX=4.58744 StartY=2.38411 StartZ=0 EndX=7.08745 EndY=2.38411 EndZ=0
  constraints (33):
    c: Vertical(g0)
    c: Vertical(g1)
    c: Distance(g1) = 2
    c: Block(g0)
    c: Block(g2)
    c: Coincident(g3,g2)
    c: Coincident(g4,g0)
    c: Coincident(g4,g3)
    c: Horizontal(g4)
    c: Block(g3)
    c: Coincident(g5,g0)
    c: Horizontal(g5)
    c: Coincident(g6,g3)
    c: Block(g6)
    c: Block(g5)
    c: Coincident(g7,g2)
    c: Block(g7)
    c: Coincident(g8,g1)
    c: Coincident(g9,g6)
    c: Vertical(g9)
    c: Coincident(g10,g7)
    c: Block(g10)
    c: Block(g8)
    c: Block(g9)
    c: Coincident(g11,g1)
    c: Vertical(g11)
    c: Distance(g11) = 1
    c: Coincident(g12,g11)
    c: Coincident(g13,g12)
    c: Coincident(g13,g7)
    c: Horizontal(g13)
    c: Block(g13)
    c: Block(g12)
FEATURE [Sketcher::SketchObject] Sketch044
  FullyConstrained = true
  MapMode = 4
  Placement = pos=(0,0,0) rot=(0.57735,0.57735,0.57735;2.0944rad)
  Support = -> [Cut014]
  sketch-geometry (14):
    g0: LineSegment StartX=6.08745 StartY=-4.11588 StartZ=0 EndX=6.08745 EndY=-2.11589 EndZ=0
    g1: LineSegment StartX=8.08745 StartY=1.38411 StartZ=0 EndX=8.08745 EndY=-1.11589 EndZ=0
    g2: ArcOfCircle CenterX=7.08745 CenterY=-1.11589 CenterZ=0 NormalX=0 NormalY=0 NormalZ=1 AngleXU=0 Radius=1 StartAngle=4.71239 EndAngle=6.28319
    g3: LineSegment StartX=6.08745 StartY=-2.11589 StartZ=0 EndX=7.08745 EndY=-2.11589 EndZ=0
    g4: LineSegment StartX=6.08745 StartY=-4.11588 StartZ=0 EndX=7.08745 EndY=-4.11588 EndZ=0
    g5: ArcOfCircle CenterX=7.08745 CenterY=-1.11589 CenterZ=0 NormalX=0 NormalY=0 NormalZ=1 AngleXU=0 Radius=3 StartAngle=4.71239 EndAngle=6.28319
    g6: ArcOfCircle CenterX=7.08745 CenterY=1.38411 CenterZ=0 NormalX=0 NormalY=0 NormalZ=1 AngleXU=0 Radius=1 StartAngle=5.35e-14 EndAngle=1.5708
    g7: LineSegment StartX=10.0875 StartY=-1.11588 StartZ=0 EndX=10.0875 EndY=1.38411 EndZ=0
    g8: ArcOfCircle CenterX=7.08745 CenterY=1.38411 CenterZ=0 NormalX=0 NormalY=0 NormalZ=1 AngleXU=0 Radius=3 StartAngle=3.57e-14 EndAngle=1.5708
    g9: ArcOfCircle CenterX=4.58745 CenterY=1.38412 CenterZ=0 NormalX=0 NormalY=0 NormalZ=1 AngleXU=0 Radius=1 StartAngle=1.57081 EndAngle=3.14159
    g10: LineSegment StartX=4.58744 StartY=2.38411 StartZ=0 EndX=7.08745 EndY=2.38411 EndZ=0
    g11: LineSegment StartX=4.58745 StartY=4.38411 StartZ=0 EndX=7.08745 EndY=4.38411 EndZ=0
    g12: ArcOfCircle CenterX=4.58745 CenterY=5.38411 CenterZ=0 NormalX=0 NormalY=0 NormalZ=1 AngleXU=0 Radius=1 StartAngle=3.14159 EndAngle=4.71239
    g13: LineSegment StartX=3.58745 StartY=5.38411 StartZ=0 EndX=3.58745 EndY=1.38411 EndZ=0
  constraints (33):
    c: Vertical(g0)
    c: Block(g0)
    c: Block(g1)
    c: Coincident(g2,g1)
    c: Coincident(g3,g0)
    c: Coincident(g3,g2)
    c: Horizontal(g3)
    c: Block(g2)
    c: Coincident(g4,g0)
    c: Horizontal(g4)
    c: Coincident(g5,g2)
    c: Block(g5)
    c: Block(g4)
    c: Coincident(g6,g1)
    c: Block(g6)
    c: Coincident(g7,g5)
    c: Vertical(g7)
    c: Coincident(g8,g6)
    c: Block(g8)
    c: Block(g7)
    c: Coincident(g10,g9)
    c: Coincident(g10,g6)
    c: Horizontal(g10)
    c: Block(g10)
    c: Block(g9)
    c: Coincident(g11,g8)
    c: Horizontal(g11)
    c: Block(g12)
    c: Block(g11)
    c: Coincident(g13,g12)
    c: Coincident(g13,g9)
    c: Vertical(g13)
    c: Tangent(g13,g9)
FEATURE [Part::Extrusion] Extrude039
  Base = -> Sketch044
  Dir = (1,0,0)
  DirMode = 2
  FaceMakerClass = Part::FaceMakerBullseye
  LengthFwd = 10
  LengthRev = 0
  Placement = pos=(8,-22.615,4.115) rot=(0,0,1;3.14159rad)
  Solid = true
  Symmetric = false
FEATURE [App::MeasureDistance] Distance004  label="Distance: 42.16 mm"
  Distance = 42.1607
  P1 = (14.6786,-26.2,1.24491)
  P2 = (-27.4815,-26.2,1.03853)
FEATURE [Sketcher::SketchObject] Sketch045
  FullyConstrained = true
  MapMode = 4
  Placement = pos=(0,0,0) rot=(0.57735,0.57735,0.57735;2.0944rad)
  Support = -> [Cut014]
  sketch-geometry (14):
    g0: LineSegment StartX=6.08745 StartY=-4.11588 StartZ=0 EndX=6.08745 EndY=-2.11589 EndZ=0
    g1: LineSegment StartX=8.08745 StartY=1.38411 StartZ=0 EndX=8.08745 EndY=-1.11589 EndZ=0
    g2: ArcOfCircle CenterX=7.08745 CenterY=-1.11589 CenterZ=0 NormalX=0 NormalY=0 NormalZ=1 AngleXU=0 Radius=1 StartAngle=4.71239 EndAngle=6.28319
    g3: LineSegment StartX=6.08745 StartY=-2.11589 StartZ=0 EndX=7.08745 EndY=-2.11589 EndZ=0
    g4: LineSegment StartX=6.08745 StartY=-4.11588 StartZ=0 EndX=7.08745 EndY=-4.11588 EndZ=0
    g5: ArcOfCircle CenterX=7.08745 CenterY=-1.11589 CenterZ=0 NormalX=0 NormalY=0 NormalZ=1 AngleXU=0 Radius=3 StartAngle=4.71239 EndAngle=6.28319
    g6: ArcOfCircle CenterX=7.08745 CenterY=1.38411 CenterZ=0 NormalX=0 NormalY=0 NormalZ=1 AngleXU=0 Radius=1 StartAngle=5.35e-14 EndAngle=1.5708
    g7: LineSegment StartX=10.0875 StartY=-1.11588 StartZ=0 EndX=10.0875 EndY=1.38411 EndZ=0
    g8: ArcOfCircle CenterX=7.08745 CenterY=1.38411 CenterZ=0 NormalX=0 NormalY=0 NormalZ=1 AngleXU=0 Radius=3 StartAngle=3.57e-14 EndAngle=1.5708
    g9: ArcOfCircle CenterX=4.58745 CenterY=1.38412 CenterZ=0 NormalX=0 NormalY=0 NormalZ=1 AngleXU=0 Radius=1 StartAngle=1.57081 EndAngle=3.14159
    g10: LineSegment StartX=4.58744 StartY=2.38411 StartZ=0 EndX=7.08745 EndY=2.38411 EndZ=0
    g11: LineSegment StartX=4.58745 StartY=4.38411 StartZ=0 EndX=7.08745 EndY=4.38411 EndZ=0
    g12: ArcOfCircle CenterX=4.58745 CenterY=5.38411 CenterZ=0 NormalX=0 NormalY=0 NormalZ=1 AngleXU=0 Radius=1 StartAngle=3.14159 EndAngle=4.71239
    g13: LineSegment StartX=3.58745 StartY=5.38411 StartZ=0 EndX=3.58745 EndY=1.38411 EndZ=0
  constraints (33):
    c: Vertical(g0)
    c: Block(g0)
    c: Block(g1)
    c: Coincident(g2,g1)
    c: Coincident(g3,g0)
    c: Coincident(g3,g2)
    c: Horizontal(g3)
    c: Block(g2)
    c: Coincident(g4,g0)
    c: Horizontal(g4)
    c: Coincident(g5,g2)
    c: Block(g5)
    c: Block(g4)
    c: Coincident(g6,g1)
    c: Block(g6)
    c: Coincident(g7,g5)
    c: Vertical(g7)
    c: Coincident(g8,g6)
    c: Block(g8)
    c: Block(g7)
    c: Coincident(g10,g9)
    c: Coincident(g10,g6)
    c: Horizontal(g10)
    c: Block(g10)
    c: Block(g9)
    c: Coincident(g11,g8)
    c: Horizontal(g11)
    c: Block(g12)
    c: Block(g11)
    c: Coincident(g13,g12)
    c: Coincident(g13,g9)
    c: Vertical(g13)
    c: Tangent(g13,g9)
FEATURE [Part::Extrusion] Extrude040
  Base = -> Sketch045
  Dir = (1,0,0)
  DirMode = 2
  FaceMakerClass = Part::FaceMakerBullseye
  LengthFwd = 10
  LengthRev = 0
  Placement = pos=(-17.5,-22.615,4.115) rot=(0,0,1;3.14159rad)
  Solid = true
  Symmetric = false
FEATURE [Sketcher::SketchObject] Sketch046
  FullyConstrained = true
  MapMode = 4
  Placement = pos=(0,0,0) rot=(0.57735,0.57735,0.57735;2.0944rad)
  Support = -> [Cut014]
  sketch-geometry (14):
    g0: LineSegment StartX=6.08745 StartY=-4.11588 StartZ=0 EndX=6.08745 EndY=-2.11589 EndZ=0
    g1: LineSegment StartX=8.08745 StartY=1.38411 StartZ=0 EndX=8.08745 EndY=-1.11589 EndZ=0
    g2: ArcOfCircle CenterX=7.08745 CenterY=-1.11589 CenterZ=0 NormalX=0 NormalY=0 NormalZ=1 AngleXU=0 Radius=1 StartAngle=4.71239 EndAngle=6.28319
    g3: LineSegment StartX=6.08745 StartY=-2.11589 StartZ=0 EndX=7.08745 EndY=-2.11589 EndZ=0
    g4: LineSegment StartX=6.08745 StartY=-4.11588 StartZ=0 EndX=7.08745 EndY=-4.11588 EndZ=0
    g5: ArcOfCircle CenterX=7.08745 CenterY=-1.11589 CenterZ=0 NormalX=0 NormalY=0 NormalZ=1 AngleXU=0 Radius=3 StartAngle=4.71239 EndAngle=6.28319
    g6: ArcOfCircle CenterX=7.08745 CenterY=1.38411 CenterZ=0 NormalX=0 NormalY=0 NormalZ=1 AngleXU=0 Radius=1 StartAngle=5.35e-14 EndAngle=1.5708
    g7: LineSegment StartX=10.0875 StartY=-1.11588 StartZ=0 EndX=10.0875 EndY=1.38411 EndZ=0
    g8: ArcOfCircle CenterX=7.08745 CenterY=1.38411 CenterZ=0 NormalX=0 NormalY=0 NormalZ=1 AngleXU=0 Radius=3 StartAngle=3.57e-14 EndAngle=1.5708
    g9: ArcOfCircle CenterX=4.58745 CenterY=1.38412 CenterZ=0 NormalX=0 NormalY=0 NormalZ=1 AngleXU=0 Radius=1 StartAngle=1.57081 EndAngle=3.14159
    g10: LineSegment StartX=4.58744 StartY=2.38411 StartZ=0 EndX=7.08745 EndY=2.38411 EndZ=0
    g11: LineSegment StartX=4.58745 StartY=4.38411 StartZ=0 EndX=7.08745 EndY=4.38411 EndZ=0
    g12: ArcOfCircle CenterX=4.58745 CenterY=5.38411 CenterZ=0 NormalX=0 NormalY=0 NormalZ=1 AngleXU=0 Radius=1 StartAngle=3.14159 EndAngle=4.71239
    g13: LineSegment StartX=3.58745 StartY=5.38411 StartZ=0 EndX=3.58745 EndY=1.38411 EndZ=0
  constraints (33):
    c: Vertical(g0)
    c: Block(g0)
    c: Block(g1)
    c: Coincident(g2,g1)
    c: Coincident(g3,g0)
    c: Coincident(g3,g2)
    c: Horizontal(g3)
    c: Block(g2)
    c: Coincident(g4,g0)
    c: Horizontal(g4)
    c: Coincident(g5,g2)
    c: Block(g5)
    c: Block(g4)
    c: Coincident(g6,g1)
    c: Block(g6)
    c: Coincident(g7,g5)
    c: Vertical(g7)
    c: Coincident(g8,g6)
    c: Block(g8)
    c: Block(g7)
    c: Coincident(g10,g9)
    c: Coincident(g10,g6)
    c: Horizontal(g10)
    c: Block(g10)
    c: Block(g9)
    c: Coincident(g11,g8)
    c: Horizontal(g11)
    c: Block(g12)
    c: Block(g11)
    c: Coincident(g13,g12)
    c: Coincident(g13,g9)
    c: Vertical(g13)
    c: Tangent(g13,g9)
FEATURE [Sketcher::SketchObject] Sketch047
  FullyConstrained = true
  MapMode = 4
  Placement = pos=(0,0,0) rot=(0.57735,0.57735,0.57735;2.0944rad)
  Support = -> [Cut014]
  sketch-geometry (14):
    g0: LineSegment StartX=6.08745 StartY=-4.11588 StartZ=0 EndX=6.08745 EndY=-2.11589 EndZ=0
    g1: LineSegment StartX=8.08745 StartY=1.38411 StartZ=0 EndX=8.08745 EndY=-1.11589 EndZ=0
    g2: ArcOfCircle CenterX=7.08745 CenterY=-1.11589 CenterZ=0 NormalX=0 NormalY=0 NormalZ=1 AngleXU=0 Radius=1 StartAngle=4.71239 EndAngle=6.28319
    g3: LineSegment StartX=6.08745 StartY=-2.11589 StartZ=0 EndX=7.08745 EndY=-2.11589 EndZ=0
    g4: LineSegment StartX=6.08745 StartY=-4.11588 StartZ=0 EndX=7.08745 EndY=-4.11588 EndZ=0
    g5: ArcOfCircle CenterX=7.08745 CenterY=-1.11589 CenterZ=0 NormalX=0 NormalY=0 NormalZ=1 AngleXU=0 Radius=3 StartAngle=4.71239 EndAngle=6.28319
    g6: ArcOfCircle CenterX=7.08745 CenterY=1.38411 CenterZ=0 NormalX=0 NormalY=0 NormalZ=1 AngleXU=0 Radius=1 StartAngle=5.35e-14 EndAngle=1.5708
    g7: LineSegment StartX=10.0875 StartY=-1.11588 StartZ=0 EndX=10.0875 EndY=1.38411 EndZ=0
    g8: ArcOfCircle CenterX=7.08745 CenterY=1.38411 CenterZ=0 NormalX=0 NormalY=0 NormalZ=1 AngleXU=0 Radius=3 StartAngle=3.57e-14 EndAngle=1.5708
    g9: ArcOfCircle CenterX=4.58745 CenterY=1.38412 CenterZ=0 NormalX=0 NormalY=0 NormalZ=1 AngleXU=0 Radius=1 StartAngle=1.57081 EndAngle=3.14159
    g10: LineSegment StartX=4.58744 StartY=2.38411 StartZ=0 EndX=7.08745 EndY=2.38411 EndZ=0
    g11: LineSegment StartX=4.58745 StartY=4.38411 StartZ=0 EndX=7.08745 EndY=4.38411 EndZ=0
    g12: ArcOfCircle CenterX=4.58745 CenterY=5.38411 CenterZ=0 NormalX=0 NormalY=0 NormalZ=1 AngleXU=0 Radius=1 StartAngle=3.14159 EndAngle=4.71239
    g13: LineSegment StartX=3.58745 StartY=5.38411 StartZ=0 EndX=3.58745 EndY=1.38411 EndZ=0
  constraints (33):
    c: Vertical(g0)
    c: Block(g0)
    c: Block(g1)
    c: Coincident(g2,g1)
    c: Coincident(g3,g0)
    c: Coincident(g3,g2)
    c: Horizontal(g3)
    c: Block(g2)
    c: Coincident(g4,g0)
    c: Horizontal(g4)
    c: Coincident(g5,g2)
    c: Block(g5)
    c: Block(g4)
    c: Coincident(g6,g1)
    c: Block(g6)
    c: Coincident(g7,g5)
    c: Vertical(g7)
    c: Coincident(g8,g6)
    c: Block(g8)
    c: Block(g7)
    c: Coincident(g10,g9)
    c: Coincident(g10,g6)
    c: Horizontal(g10)
    c: Block(g10)
    c: Block(g9)
    c: Coincident(g11,g8)
    c: Horizontal(g11)
    c: Block(g12)
    c: Block(g11)
    c: Coincident(g13,g12)
    c: Coincident(g13,g9)
    c: Vertical(g13)
    c: Tangent(g13,g9)
FEATURE [Sketcher::SketchObject] Sketch048
  FullyConstrained = true
  MapMode = 4
  Placement = pos=(0,0,0) rot=(0.57735,0.57735,0.57735;2.0944rad)
  Support = -> [Cut014]
  sketch-geometry (14):
    g0: LineSegment StartX=6.08745 StartY=-4.11588 StartZ=0 EndX=6.08745 EndY=-2.11589 EndZ=0
    g1: LineSegment StartX=8.08745 StartY=1.38411 StartZ=0 EndX=8.08745 EndY=-1.11589 EndZ=0
    g2: ArcOfCircle CenterX=7.08745 CenterY=-1.11589 CenterZ=0 NormalX=0 NormalY=0 NormalZ=1 AngleXU=0 Radius=1 StartAngle=4.71239 EndAngle=6.28319
    g3: LineSegment StartX=6.08745 StartY=-2.11589 StartZ=0 EndX=7.08745 EndY=-2.11589 EndZ=0
    g4: LineSegment StartX=6.08745 StartY=-4.11588 StartZ=0 EndX=7.08745 EndY=-4.11588 EndZ=0
    g5: ArcOfCircle CenterX=7.08745 CenterY=-1.11589 CenterZ=0 NormalX=0 NormalY=0 NormalZ=1 AngleXU=0 Radius=3 StartAngle=4.71239 EndAngle=6.28319
    g6: ArcOfCircle CenterX=7.08745 CenterY=1.38411 CenterZ=0 NormalX=0 NormalY=0 NormalZ=1 AngleXU=0 Radius=1 StartAngle=5.35e-14 EndAngle=1.5708
    g7: LineSegment StartX=10.0875 StartY=-1.11588 StartZ=0 EndX=10.0875 EndY=1.38411 EndZ=0
    g8: ArcOfCircle CenterX=7.08745 CenterY=1.38411 CenterZ=0 NormalX=0 NormalY=0 NormalZ=1 AngleXU=0 Radius=3 StartAngle=3.57e-14 EndAngle=1.5708
    g9: ArcOfCircle CenterX=4.58745 CenterY=1.38412 CenterZ=0 NormalX=0 NormalY=0 NormalZ=1 AngleXU=0 Radius=1 StartAngle=1.57081 EndAngle=3.14159
    g10: LineSegment StartX=4.58744 StartY=2.38411 StartZ=0 EndX=7.08745 EndY=2.38411 EndZ=0
    g11: LineSegment StartX=4.58745 StartY=4.38411 StartZ=0 EndX=7.08745 EndY=4.38411 EndZ=0
    g12: ArcOfCircle CenterX=4.58745 CenterY=5.38411 CenterZ=0 NormalX=0 NormalY=0 NormalZ=1 AngleXU=0 Radius=1 StartAngle=3.14159 EndAngle=4.71239
    g13: LineSegment StartX=3.58745 StartY=5.38411 StartZ=0 EndX=3.58745 EndY=1.38411 EndZ=0
  constraints (33):
    c: Vertical(g0)
    c: Block(g0)
    c: Block(g1)
    c: Coincident(g2,g1)
    c: Coincident(g3,g0)
    c: Coincident(g3,g2)
    c: Horizontal(g3)
    c: Block(g2)
    c: Coincident(g4,g0)
    c: Horizontal(g4)
    c: Coincident(g5,g2)
    c: Block(g5)
    c: Block(g4)
    c: Coincident(g6,g1)
    c: Block(g6)
    c: Coincident(g7,g5)
    c: Vertical(g7)
    c: Coincident(g8,g6)
    c: Block(g8)
    c: Block(g7)
    c: Coincident(g10,g9)
    c: Coincident(g10,g6)
    c: Horizontal(g10)
    c: Block(g10)
    c: Block(g9)
    c: Coincident(g11,g8)
    c: Horizontal(g11)
    c: Block(g12)
    c: Block(g11)
    c: Coincident(g13,g12)
    c: Coincident(g13,g9)
    c: Vertical(g13)
    c: Tangent(g13,g9)
FEATURE [Sketcher::SketchObject] Sketch049
  FullyConstrained = true
  MapMode = 4
  Placement = pos=(0,0,0) rot=(0.57735,0.57735,0.57735;2.0944rad)
  Support = -> [Cut014]
  sketch-geometry (14):
    g0: LineSegment StartX=6.08745 StartY=-4.11588 StartZ=0 EndX=6.08745 EndY=-2.11589 EndZ=0
    g1: LineSegment StartX=8.08745 StartY=1.38411 StartZ=0 EndX=8.08745 EndY=-1.11589 EndZ=0
    g2: ArcOfCircle CenterX=7.08745 CenterY=-1.11589 CenterZ=0 NormalX=0 NormalY=0 NormalZ=1 AngleXU=0 Radius=1 StartAngle=4.71239 EndAngle=6.28319
    g3: LineSegment StartX=6.08745 StartY=-2.11589 StartZ=0 EndX=7.08745 EndY=-2.11589 EndZ=0
    g4: LineSegment StartX=6.08745 StartY=-4.11588 StartZ=0 EndX=7.08745 EndY=-4.11588 EndZ=0
    g5: ArcOfCircle CenterX=7.08745 CenterY=-1.11589 CenterZ=0 NormalX=0 NormalY=0 NormalZ=1 AngleXU=0 Radius=3 StartAngle=4.71239 EndAngle=6.28319
    g6: ArcOfCircle CenterX=7.08745 CenterY=1.38411 CenterZ=0 NormalX=0 NormalY=0 NormalZ=1 AngleXU=0 Radius=1 StartAngle=5.35e-14 EndAngle=1.5708
    g7: LineSegment StartX=10.0875 StartY=-1.11588 StartZ=0 EndX=10.0875 EndY=1.38411 EndZ=0
    g8: ArcOfCircle CenterX=7.08745 CenterY=1.38411 CenterZ=0 NormalX=0 NormalY=0 NormalZ=1 AngleXU=0 Radius=3 StartAngle=3.57e-14 EndAngle=1.5708
    g9: ArcOfCircle CenterX=4.58745 CenterY=1.38412 CenterZ=0 NormalX=0 NormalY=0 NormalZ=1 AngleXU=0 Radius=1 StartAngle=1.57081 EndAngle=3.14159
    g10: LineSegment StartX=4.58744 StartY=2.38411 StartZ=0 EndX=7.08745 EndY=2.38411 EndZ=0
    g11: LineSegment StartX=4.58745 StartY=4.38411 StartZ=0 EndX=7.08745 EndY=4.38411 EndZ=0
    g12: ArcOfCircle CenterX=4.58745 CenterY=5.38411 CenterZ=0 NormalX=0 NormalY=0 NormalZ=1 AngleXU=0 Radius=1 StartAngle=3.14159 EndAngle=4.71239
    g13: LineSegment StartX=3.58745 StartY=5.38411 StartZ=0 EndX=3.58745 EndY=1.38411 EndZ=0
  constraints (33):
    c: Vertical(g0)
    c: Block(g0)
    c: Block(g1)
    c: Coincident(g2,g1)
    c: Coincident(g3,g0)
    c: Coincident(g3,g2)
    c: Horizontal(g3)
    c: Block(g2)
    c: Coincident(g4,g0)
    c: Horizontal(g4)
    c: Coincident(g5,g2)
    c: Block(g5)
    c: Block(g4)
    c: Coincident(g6,g1)
    c: Block(g6)
    c: Coincident(g7,g5)
    c: Vertical(g7)
    c: Coincident(g8,g6)
    c: Block(g8)
    c: Block(g7)
    c: Coincident(g10,g9)
    c: Coincident(g10,g6)
    c: Horizontal(g10)
    c: Block(g10)
    c: Block(g9)
    c: Coincident(g11,g8)
    c: Horizontal(g11)
    c: Block(g12)
    c: Block(g11)
    c: Coincident(g13,g12)
    c: Coincident(g13,g9)
    c: Vertical(g13)
    c: Tangent(g13,g9)
FEATURE [Part::Extrusion] Extrude041
  Base = -> Sketch049
  Dir = (1,0,0)
  DirMode = 2
  FaceMakerClass = Part::FaceMakerBullseye
  LengthFwd = 10
  LengthRev = 0
  Placement = pos=(-2,-22.615,14.6) rot=(0,0,1;3.14159rad)
  Solid = true
  Symmetric = false
FEATURE [Part::MultiFuse] Fusion023
  Shapes = -> [Extrude039,Extrude040,Extrude041,Cut014,Fusion015]
FEATURE [Part::Extrusion] Extrude042
  Base = -> Sketch034
  Dir = (0,0.894389,-0.447291)
  DirMode = 2
  FaceMakerClass = Part::FaceMakerBullseye
  LengthFwd = 14
  LengthRev = 0
  Placement = pos=(45.5,-14,12.7) rot=(1,0,0;0.466003rad)
  Solid = true
  Symmetric = false
FEATURE [Part::Box] Box014  label="Cube014"
  AttacherType = Attacher::AttachEngine3D
  Height = 2
  Length = 2
  Placement = pos=(-12.85,-28.2,0) rot=(0,0,1;0rad)
  Width = 2
FEATURE [App::MeasureDistance] Distance005  label="Distance: 15.50 mm"
  Distance = 15.5
  P1 = (-17.5,-32.7025,2.99911)
  P2 = (-2,-32.7025,2.99911)
FEATURE [Part::Box] Box015  label="Cube015"
  AttacherType = Attacher::AttachEngine3D
  Height = 2
  Length = 2
  Placement = pos=(-10.85,-28.2,0) rot=(0,0,1;0rad)
  Width = 2
FEATURE [Part::MultiFuse] Fusion024  label="wireHoldersecondery024"
  Placement = pos=(-8.65,0,10.48) rot=(0,0,1;0rad)
  Shapes = -> [Box015,Box014]
FEATURE [App::MeasureDistance] Distance006  label="Distance: 9.44 mm"
  Distance = 9.44274
  P1 = (-8.85,-28.2,0)
  P2 = (-2,-28.1337,6.49911)
FEATURE [Part::Box] Box016  label="Cube016"
  AttacherType = Attacher::AttachEngine3D
  Height = 2
  Length = 2
  Placement = pos=(-12.85,-28.2,0) rot=(0,0,1;0rad)
  Width = 2
FEATURE [Part::Box] Box017  label="Cube017"
  AttacherType = Attacher::AttachEngine3D
  Height = 2
  Length = 2
  Placement = pos=(-10.85,-28.2,0) rot=(0,0,1;0rad)
  Width = 2
FEATURE [Part::MultiFuse] Fusion025  label="wireHoldersecondery025"
  Placement = pos=(1,0,0) rot=(0,0,1;0rad)
  Shapes = -> [Box017,Box016]
FEATURE [App::MeasureDistance] Distance007  label="Distance: 1.58 mm"
  Distance = 1.582
  P1 = (-12,-28.7025,10.4841)
  P2 = (-13.5,-28.2,10.5)
FEATURE [App::MeasureDistance] Distance008  label="Distance: 1.58 mm001"
  Distance = 1.58193
  P1 = (-13.5,-28.2,10.49)
  P2 = (-12,-28.7025,10.4841)
FEATURE [App::MeasureDistance] Distance009  label="Distance: 1.58 mm002"
  Distance = 1.58192
  P1 = (-13.5,-28.2,10.48)
  P2 = (-12,-28.7025,10.4841)
FEATURE [Part::Box] Box018  label="Cube018"
  AttacherType = Attacher::AttachEngine3D
  Height = 6.5
  Length = 8
  Placement = pos=(44,-23,2.4) rot=(0,0,1;0rad)
  Width = 6
FEATURE [Sketcher::SketchObject] Sketch050
  FullyConstrained = true
  Placement = pos=(0,-14.3,2.37) rot=(-1,0,0;2.03453rad)
  sketch-geometry (4):
    g0: LineSegment StartX=0 StartY=1.5 StartZ=0 EndX=4 EndY=1.5 EndZ=0
    g1: LineSegment StartX=4 StartY=1.5 StartZ=0 EndX=4 EndY=-2.5 EndZ=0
    g2: LineSegment StartX=4 StartY=-2.5 StartZ=0 EndX=0 EndY=-2.5 EndZ=0
    g3: LineSegment StartX=0 StartY=1.5 StartZ=0 EndX=0 EndY=-2.5 EndZ=0
  constraints (11):
    c: Horizontal(g0)
    c: Distance(g0) = 4
    c: Block(g0)
    c: Coincident(g1,g0)
    c: Vertical(g1)
    c: Distance(g1) = 4
    c: Coincident(g2,g1)
    c: Horizontal(g2)
    c: Distance(g2) = 4
    c: Coincident(g3,g0)
    c: Coincident(g3,g2)
FEATURE [Part::Cut] Cut015
  Base = -> Fusion023
  Tool = -> Box018
FEATURE [Part::Fillet] Fillet021
  Base = -> Extrude042
  Edges = 1 edges r=2: [Edge2]
FEATURE [Part::Fillet] Fillet022
  Base = -> Cut015
  Edges = 1 edges r=2: [Edge528]
FEATURE [Part::Fillet] Fillet023
  Base = -> Fillet021
  Edges = 1 edges r=1.4: [Edge12]
